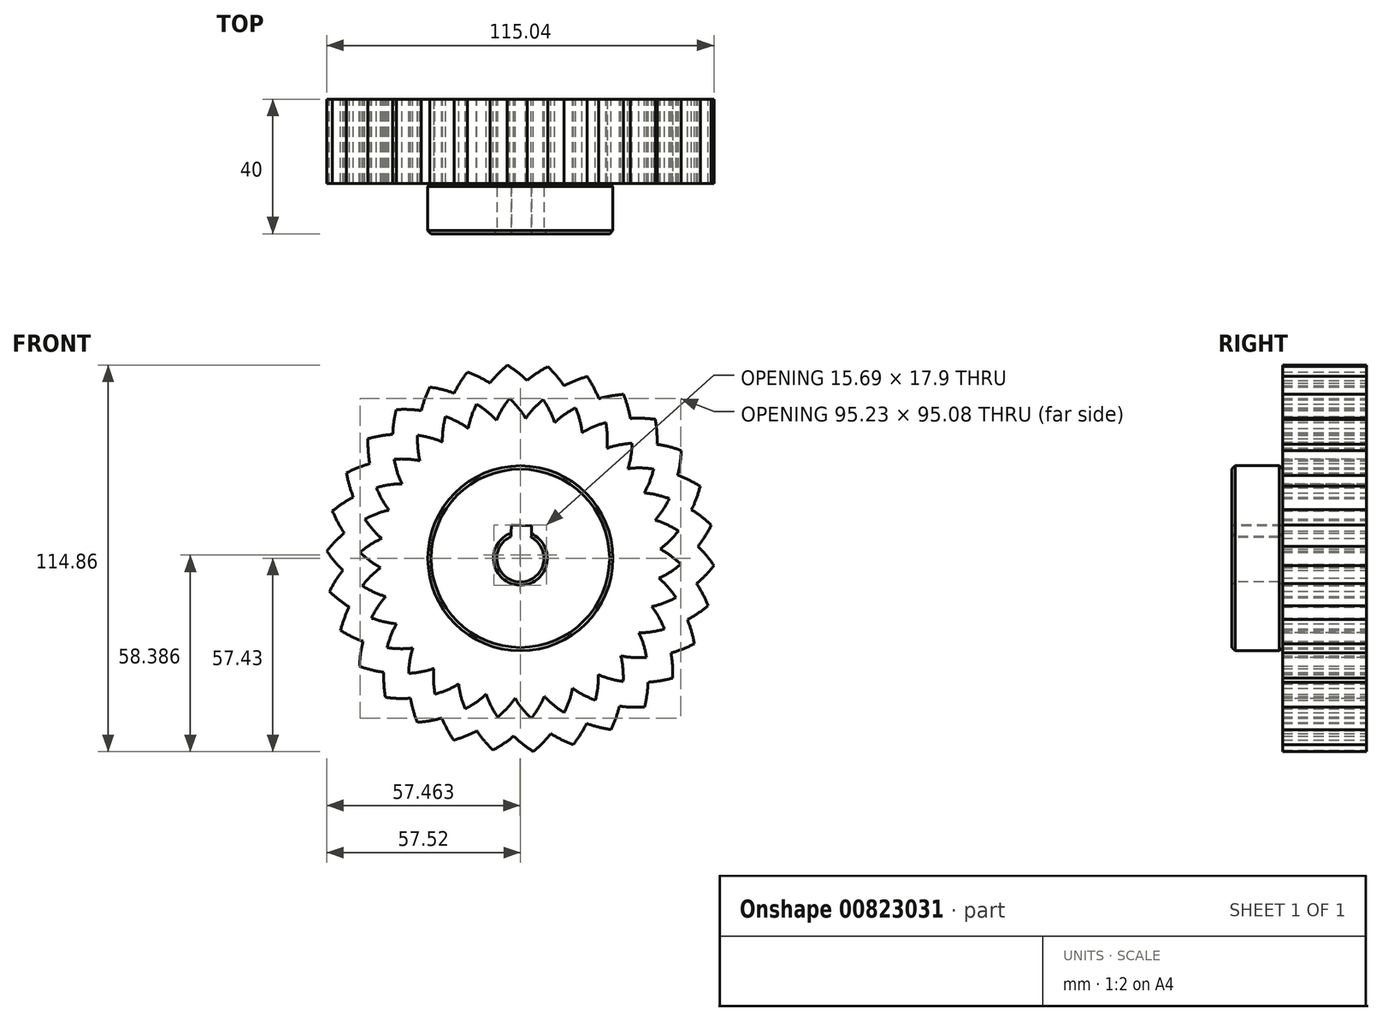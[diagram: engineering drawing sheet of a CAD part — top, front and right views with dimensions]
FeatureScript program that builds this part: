
annotation { "Feature Type Name" : "Feature", "Feature Type Description" : "" }
export const myFeature = defineFeature(function(context is Context, id is Id, definition is map)
    precondition{}
    {
        {
            var Q0;
            Q0=qCreatedBy(makeId("Front.planeOp"),FACE);
            var sketch = newSketch(context, id + "F0", { "sketchPlane" : qUnion([Q0])});
            skArc(sketch, "E0", {"start": v(-34.7, 6.12) * mm, "mid": v(-35.1, 3.07) * mm, "end": v(-35.24, 0) * mm, "construction": true});
            skLineSegment(sketch, "E1", {"start": v(0, 0) * mm, "end": v(309.01, 0) * mm, "construction": true});
            skPoint(sketch, "E2", {"position": v(35.24, 0) * mm});
            skLineSegment(sketch, "E3", {"start": v(0, 0) * mm, "end": v(-35.24, 0) * mm, "construction": true});
            skArc(sketch, "E4.trimOffspring", {"start": v(-30.6, -17.46) * mm, "mid": v(35.03, 3.83) * mm, "end": v(-33.66, 10.43) * mm, "construction": true});
            skFitSpline(sketch, "E5", {"points": [v(35.24, 0) * mm, v(35.77, 0.06) * mm, v(37.32, 0.5) * mm, v(39.74, 1.64) * mm, v(42.8, 3.8) * mm, v(46.2, 7.23) * mm, v(49.58, 12.07) * mm, v(52.5, 18.39) * mm, v(54.57, 26.16) * mm], "startDerivative": vector(10.04, 0.75) * mm, "endDerivative": vector(10.04, 44.08) * mm});
            skArc(sketch, "E6", {"start": v(34.12, 5.1) * mm, "mid": v(34, 5.9) * mm, "end": v(33.85, 6.7) * mm});
            skArc(sketch, "E7", {"start": v(39.96, 1.77) * mm, "mid": v(39.9, 2.68) * mm, "end": v(39.84, 3.6) * mm});
            skCircle(sketch, "E8", {"center": v(0, 0) * mm, "radius": 37.5 * mm, "construction": true});
            skPoint(sketch, "E9", {"position": v(37.5, 0.56) * mm});
            skPoint(sketch, "E10", {"position": v(36.56, 8.34) * mm});
            skPoint(sketch, "E11.orphan", {"position": v(37.03, 4.45) * mm});
            skLineSegment(sketch, "E12", {"start": v(37.5, 0.56) * mm, "end": v(37.03, 4.45) * mm, "construction": true});
            skLineSegment(sketch, "E13", {"start": v(37.26, 2.5) * mm, "end": v(0, 0) * mm, "construction": true});
            skFitSpline(sketch, "E14.MirrorCS", {"points": [v(34.92, 4.72) * mm, v(35.46, 4.73) * mm, v(37.05, 4.5) * mm, v(39.6, 3.7) * mm, v(42.93, 1.96) * mm, v(46.76, -0.98) * mm, v(50.74, -5.32) * mm, v(54.5, -11.2) * mm, v(57.58, -18.62) * mm], "startDerivative": vector(10.05, 0.6) * mm, "endDerivative": vector(15.85, -42.34) * mm});
            skLineSegment(sketch, "E15", {"start": v(35.24, 0) * mm, "end": v(35, 0) * mm});
            skLineSegment(sketch, "E16.MirrorCS", {"start": v(34.92, 4.72) * mm, "end": v(34.68, 4.68) * mm});
            skPoint(sketch, "E17.visualSharp", {"position": v(34.19, 4.62) * mm});
            skArc(sketch, "E17.filletArc", {"start": v(34.12, 5.1) * mm, "mid": v(34.31, 4.78) * mm, "end": v(34.68, 4.68) * mm});
            skPoint(sketch, "E18.visualSharp", {"position": v(34.5, 0) * mm});
            skArc(sketch, "E18.filletArc", {"start": v(35, 0) * mm, "mid": v(34.65, -0.14) * mm, "end": v(34.5, -0.5) * mm});
            skPoint(sketch, "E19.1.1", {"position": v(34.47, 7.33) * mm});
            skPoint(sketch, "E19.1.2", {"position": v(33.75, 7.17) * mm});
            skPoint(sketch, "E19.1.3", {"position": v(32.48, 11.62) * mm});
            skPoint(sketch, "E19.1.4", {"position": v(35.3, 12.05) * mm});
            skPoint(sketch, "E19.1.5", {"position": v(33.18, 11.87) * mm});
            skArc(sketch, "E19.1.6", {"start": v(38.72, 10.04) * mm, "mid": v(38.48, 10.92) * mm, "end": v(38.22, 11.8) * mm});
            skArc(sketch, "E19.1.8", {"start": v(32.31, 12.09) * mm, "mid": v(32.57, 11.8) * mm, "end": v(32.95, 11.8) * mm});
            skPoint(sketch, "E19.1.9", {"position": v(34.47, 7.33) * mm});
            skPoint(sketch, "E19.1.10", {"position": v(33.18, 11.87) * mm});
            skArc(sketch, "E19.1.11", {"start": v(34.23, 7.28) * mm, "mid": v(33.92, 7.06) * mm, "end": v(33.85, 6.7) * mm});
            skPoint(sketch, "E19.1.12", {"position": v(33.18, 11.87) * mm});
            skPoint(sketch, "E19.1.13", {"position": v(34.47, 7.33) * mm});
            skPoint(sketch, "E19.1.14", {"position": v(33.18, 11.87) * mm});
            skPoint(sketch, "E19.1.15", {"position": v(34.47, 7.33) * mm});
            skPoint(sketch, "E19.1.16", {"position": v(34.47, 7.33) * mm});
            skPoint(sketch, "E19.1.17", {"position": v(33.18, 11.87) * mm});
            skPoint(sketch, "E19.1.18", {"position": v(33.18, 11.87) * mm});
            skPoint(sketch, "E19.1.19", {"position": v(34.47, 7.33) * mm});
            skPoint(sketch, "E19.1.20", {"position": v(33.18, 11.87) * mm});
            skPoint(sketch, "E19.1.21", {"position": v(34.47, 7.33) * mm});
            skPoint(sketch, "E19.1.22", {"position": v(33.18, 11.87) * mm});
            skPoint(sketch, "E19.1.23", {"position": v(34.47, 7.33) * mm});
            skLineSegment(sketch, "E19.1.24", {"start": v(33.18, 11.87) * mm, "end": v(32.95, 11.8) * mm});
            skLineSegment(sketch, "E19.1.25", {"start": v(34.47, 7.33) * mm, "end": v(34.23, 7.28) * mm});
            skPoint(sketch, "E19.2.1", {"position": v(32.2, 14.33) * mm});
            skPoint(sketch, "E19.2.2", {"position": v(31.52, 14.03) * mm});
            skPoint(sketch, "E19.2.3", {"position": v(29.36, 18.12) * mm});
            skPoint(sketch, "E19.2.4", {"position": v(32.02, 19.13) * mm});
            skPoint(sketch, "E19.2.5", {"position": v(29.98, 18.51) * mm});
            skArc(sketch, "E19.2.6", {"start": v(35.79, 17.87) * mm, "mid": v(35.37, 18.68) * mm, "end": v(34.93, 19.49) * mm});
            skPoint(sketch, "E19.2.7", {"position": v(34.03, 15.76) * mm});
            skArc(sketch, "E19.2.8", {"start": v(29.1, 18.54) * mm, "mid": v(29.4, 18.32) * mm, "end": v(29.78, 18.38) * mm});
            skPoint(sketch, "E19.2.9", {"position": v(32.2, 14.33) * mm});
            skPoint(sketch, "E19.2.10", {"position": v(29.98, 18.51) * mm});
            skArc(sketch, "E19.2.11", {"start": v(31.97, 14.23) * mm, "mid": v(31.7, 13.96) * mm, "end": v(31.71, 13.58) * mm});
            skPoint(sketch, "E19.2.12", {"position": v(29.98, 18.51) * mm});
            skPoint(sketch, "E19.2.13", {"position": v(32.2, 14.33) * mm});
            skPoint(sketch, "E19.2.14", {"position": v(29.98, 18.51) * mm});
            skPoint(sketch, "E19.2.15", {"position": v(32.2, 14.33) * mm});
            skPoint(sketch, "E19.2.16", {"position": v(32.2, 14.33) * mm});
            skPoint(sketch, "E19.2.17", {"position": v(29.98, 18.51) * mm});
            skPoint(sketch, "E19.2.18", {"position": v(29.98, 18.51) * mm});
            skPoint(sketch, "E19.2.19", {"position": v(32.2, 14.33) * mm});
            skPoint(sketch, "E19.2.20", {"position": v(29.98, 18.51) * mm});
            skPoint(sketch, "E19.2.21", {"position": v(32.2, 14.33) * mm});
            skPoint(sketch, "E19.2.22", {"position": v(29.98, 18.51) * mm});
            skPoint(sketch, "E19.2.23", {"position": v(32.2, 14.33) * mm});
            skLineSegment(sketch, "E19.2.24", {"start": v(29.98, 18.51) * mm, "end": v(29.78, 18.38) * mm});
            skLineSegment(sketch, "E19.2.25", {"start": v(32.2, 14.33) * mm, "end": v(31.97, 14.23) * mm});
            skLineSegment(sketch, "E19.3.0", {"start": v(30, 22.5) * mm, "end": v(27.34, 25.37) * mm, "construction": true});
            skPoint(sketch, "E19.3.1", {"position": v(28.5, 20.71) * mm});
            skPoint(sketch, "E19.3.2", {"position": v(27.91, 20.28) * mm});
            skPoint(sketch, "E19.3.3", {"position": v(24.95, 23.83) * mm});
            skPoint(sketch, "E19.3.4", {"position": v(27.34, 25.37) * mm});
            skPoint(sketch, "E19.3.5", {"position": v(25.48, 24.34) * mm});
            skArc(sketch, "E19.3.6", {"start": v(31.29, 24.92) * mm, "mid": v(30.71, 25.63) * mm, "end": v(30.12, 26.32) * mm});
            skPoint(sketch, "E19.3.7", {"position": v(30, 22.5) * mm});
            skArc(sketch, "E19.3.8", {"start": v(24.6, 24.19) * mm, "mid": v(24.95, 24.04) * mm, "end": v(25.3, 24.17) * mm});
            skPoint(sketch, "E19.3.9", {"position": v(28.5, 20.71) * mm});
            skPoint(sketch, "E19.3.10", {"position": v(25.48, 24.34) * mm});
            skArc(sketch, "E19.3.11", {"start": v(28.31, 20.57) * mm, "mid": v(28.11, 20.25) * mm, "end": v(28.2, 19.88) * mm});
            skPoint(sketch, "E19.3.12", {"position": v(25.48, 24.34) * mm});
            skPoint(sketch, "E19.3.13", {"position": v(28.5, 20.71) * mm});
            skPoint(sketch, "E19.3.14", {"position": v(25.48, 24.34) * mm});
            skPoint(sketch, "E19.3.15", {"position": v(28.5, 20.71) * mm});
            skPoint(sketch, "E19.3.16", {"position": v(28.5, 20.71) * mm});
            skPoint(sketch, "E19.3.17", {"position": v(25.48, 24.34) * mm});
            skPoint(sketch, "E19.3.18", {"position": v(25.48, 24.34) * mm});
            skPoint(sketch, "E19.3.19", {"position": v(28.5, 20.71) * mm});
            skPoint(sketch, "E19.3.20", {"position": v(25.48, 24.34) * mm});
            skPoint(sketch, "E19.3.21", {"position": v(28.5, 20.71) * mm});
            skPoint(sketch, "E19.3.22", {"position": v(25.48, 24.34) * mm});
            skPoint(sketch, "E19.3.23", {"position": v(28.5, 20.71) * mm});
            skLineSegment(sketch, "E19.3.24", {"start": v(25.48, 24.34) * mm, "end": v(25.3, 24.17) * mm});
            skLineSegment(sketch, "E19.3.25", {"start": v(28.5, 20.71) * mm, "end": v(28.31, 20.57) * mm});
            skLineSegment(sketch, "E19.4.0", {"start": v(24.67, 28.24) * mm, "end": v(21.47, 30.5) * mm, "construction": true});
            skPoint(sketch, "E19.4.1", {"position": v(23.58, 26.19) * mm});
            skPoint(sketch, "E19.4.2", {"position": v(23.09, 25.64) * mm});
            skPoint(sketch, "E19.4.3", {"position": v(19.45, 28.5) * mm});
            skPoint(sketch, "E19.4.4", {"position": v(21.47, 30.5) * mm});
            skPoint(sketch, "E19.4.5", {"position": v(19.86, 29.1) * mm});
            skArc(sketch, "E19.4.6", {"start": v(25.42, 30.88) * mm, "mid": v(24.71, 31.45) * mm, "end": v(23.99, 32.01) * mm});
            skPoint(sketch, "E19.4.7", {"position": v(24.67, 28.24) * mm});
            skArc(sketch, "E19.4.8", {"start": v(19.04, 28.77) * mm, "mid": v(19.4, 28.7) * mm, "end": v(19.73, 28.9) * mm});
            skPoint(sketch, "E19.4.9", {"position": v(23.58, 26.19) * mm});
            skPoint(sketch, "E19.4.10", {"position": v(19.86, 29.1) * mm});
            skArc(sketch, "E19.4.11", {"start": v(23.42, 26) * mm, "mid": v(23.29, 25.65) * mm, "end": v(23.45, 25.3) * mm});
            skPoint(sketch, "E19.4.12", {"position": v(19.86, 29.1) * mm});
            skPoint(sketch, "E19.4.13", {"position": v(23.58, 26.19) * mm});
            skPoint(sketch, "E19.4.14", {"position": v(19.86, 29.1) * mm});
            skPoint(sketch, "E19.4.15", {"position": v(23.58, 26.19) * mm});
            skPoint(sketch, "E19.4.16", {"position": v(23.58, 26.19) * mm});
            skPoint(sketch, "E19.4.17", {"position": v(19.86, 29.1) * mm});
            skPoint(sketch, "E19.4.18", {"position": v(19.86, 29.1) * mm});
            skPoint(sketch, "E19.4.19", {"position": v(23.58, 26.19) * mm});
            skPoint(sketch, "E19.4.20", {"position": v(19.86, 29.1) * mm});
            skPoint(sketch, "E19.4.21", {"position": v(23.58, 26.19) * mm});
            skPoint(sketch, "E19.4.22", {"position": v(19.86, 29.1) * mm});
            skPoint(sketch, "E19.4.23", {"position": v(23.58, 26.19) * mm});
            skLineSegment(sketch, "E19.4.24", {"start": v(19.86, 29.1) * mm, "end": v(19.73, 28.9) * mm});
            skLineSegment(sketch, "E19.4.25", {"start": v(23.58, 26.19) * mm, "end": v(23.42, 26) * mm});
            skLineSegment(sketch, "E19.5.0", {"start": v(18.26, 32.75) * mm, "end": v(14.66, 34.3) * mm, "construction": true});
            skPoint(sketch, "E19.5.1", {"position": v(17.62, 30.52) * mm});
            skPoint(sketch, "E19.5.2", {"position": v(17.25, 29.88) * mm});
            skPoint(sketch, "E19.5.3", {"position": v(13.1, 31.92) * mm});
            skPoint(sketch, "E19.5.4", {"position": v(14.66, 34.3) * mm});
            skPoint(sketch, "E19.5.5", {"position": v(13.38, 32.6) * mm});
            skArc(sketch, "E19.5.6", {"start": v(18.45, 35.5) * mm, "mid": v(17.63, 35.9) * mm, "end": v(16.8, 36.3) * mm});
            skPoint(sketch, "E19.5.7", {"position": v(18.26, 32.75) * mm});
            skArc(sketch, "E19.5.8", {"start": v(12.64, 32.1) * mm, "mid": v(13.02, 32.1) * mm, "end": v(13.28, 32.38) * mm});
            skPoint(sketch, "E19.5.9", {"position": v(17.62, 30.52) * mm});
            skPoint(sketch, "E19.5.10", {"position": v(13.38, 32.6) * mm});
            skArc(sketch, "E19.5.11", {"start": v(17.5, 30.3) * mm, "mid": v(17.45, 29.93) * mm, "end": v(17.68, 29.63) * mm});
            skPoint(sketch, "E19.5.12", {"position": v(13.38, 32.6) * mm});
            skPoint(sketch, "E19.5.13", {"position": v(17.62, 30.52) * mm});
            skPoint(sketch, "E19.5.14", {"position": v(13.38, 32.6) * mm});
            skPoint(sketch, "E19.5.15", {"position": v(17.62, 30.52) * mm});
            skPoint(sketch, "E19.5.16", {"position": v(17.62, 30.52) * mm});
            skPoint(sketch, "E19.5.17", {"position": v(13.38, 32.6) * mm});
            skPoint(sketch, "E19.5.18", {"position": v(13.38, 32.6) * mm});
            skPoint(sketch, "E19.5.19", {"position": v(17.62, 30.52) * mm});
            skPoint(sketch, "E19.5.20", {"position": v(13.38, 32.6) * mm});
            skPoint(sketch, "E19.5.21", {"position": v(17.62, 30.52) * mm});
            skPoint(sketch, "E19.5.22", {"position": v(13.38, 32.6) * mm});
            skPoint(sketch, "E19.5.23", {"position": v(17.62, 30.52) * mm});
            skLineSegment(sketch, "E19.5.24", {"start": v(13.38, 32.6) * mm, "end": v(13.28, 32.38) * mm});
            skLineSegment(sketch, "E19.5.25", {"start": v(17.62, 30.52) * mm, "end": v(17.5, 30.3) * mm});
            skLineSegment(sketch, "E19.6.0", {"start": v(11.06, 35.83) * mm, "end": v(7.2, 36.6) * mm, "construction": true});
            skPoint(sketch, "E19.6.1", {"position": v(10.89, 33.51) * mm});
            skPoint(sketch, "E19.6.2", {"position": v(10.66, 32.81) * mm});
            skPoint(sketch, "E19.6.3", {"position": v(6.17, 33.94) * mm});
            skPoint(sketch, "E19.6.4", {"position": v(7.2, 36.6) * mm});
            skPoint(sketch, "E19.6.5", {"position": v(6.3, 34.67) * mm});
            skArc(sketch, "E19.6.6", {"start": v(10.67, 38.55) * mm, "mid": v(9.78, 38.79) * mm, "end": v(8.9, 39) * mm});
            skPoint(sketch, "E19.6.7", {"position": v(11.06, 35.83) * mm});
            skArc(sketch, "E19.6.8", {"start": v(5.69, 34.03) * mm, "mid": v(6.06, 34.11) * mm, "end": v(6.26, 34.43) * mm});
            skPoint(sketch, "E19.6.9", {"position": v(10.89, 33.51) * mm});
            skPoint(sketch, "E19.6.10", {"position": v(6.3, 34.67) * mm});
            skArc(sketch, "E19.6.11", {"start": v(10.81, 33.28) * mm, "mid": v(10.84, 32.9) * mm, "end": v(11.13, 32.66) * mm});
            skPoint(sketch, "E19.6.12", {"position": v(6.3, 34.67) * mm});
            skPoint(sketch, "E19.6.13", {"position": v(10.89, 33.51) * mm});
            skPoint(sketch, "E19.6.14", {"position": v(6.3, 34.67) * mm});
            skPoint(sketch, "E19.6.15", {"position": v(10.89, 33.51) * mm});
            skPoint(sketch, "E19.6.16", {"position": v(10.89, 33.51) * mm});
            skPoint(sketch, "E19.6.17", {"position": v(6.3, 34.67) * mm});
            skPoint(sketch, "E19.6.18", {"position": v(6.3, 34.67) * mm});
            skPoint(sketch, "E19.6.19", {"position": v(10.89, 33.51) * mm});
            skPoint(sketch, "E19.6.20", {"position": v(6.3, 34.67) * mm});
            skPoint(sketch, "E19.6.21", {"position": v(10.89, 33.51) * mm});
            skPoint(sketch, "E19.6.22", {"position": v(6.3, 34.67) * mm});
            skPoint(sketch, "E19.6.23", {"position": v(10.89, 33.51) * mm});
            skLineSegment(sketch, "E19.6.24", {"start": v(6.3, 34.67) * mm, "end": v(6.26, 34.43) * mm});
            skLineSegment(sketch, "E19.6.25", {"start": v(10.89, 33.51) * mm, "end": v(10.81, 33.28) * mm});
            skLineSegment(sketch, "E19.7.0", {"start": v(3.36, 37.35) * mm, "end": v(-0.56, 37.3) * mm, "construction": true});
            skPoint(sketch, "E19.7.1", {"position": v(3.68, 35.05) * mm});
            skPoint(sketch, "E19.7.2", {"position": v(3.6, 34.31) * mm});
            skPoint(sketch, "E19.7.3", {"position": v(-1.02, 34.48) * mm});
            skPoint(sketch, "E19.7.4", {"position": v(-0.56, 37.3) * mm});
            skPoint(sketch, "E19.7.5", {"position": v(-1.04, 35.22) * mm});
            skArc(sketch, "E19.7.6", {"start": v(2.42, 39.93) * mm, "mid": v(1.5, 39.97) * mm, "end": v(0.6, 40) * mm});
            skPoint(sketch, "E19.7.7", {"position": v(3.36, 37.35) * mm});
            skArc(sketch, "E19.7.8", {"start": v(-1.51, 34.47) * mm, "mid": v(-1.17, 34.63) * mm, "end": v(-1.03, 34.98) * mm});
            skPoint(sketch, "E19.7.9", {"position": v(3.68, 35.05) * mm});
            skPoint(sketch, "E19.7.10", {"position": v(-1.04, 35.22) * mm});
            skArc(sketch, "E19.7.11", {"start": v(3.66, 34.8) * mm, "mid": v(3.76, 34.44) * mm, "end": v(4.1, 34.26) * mm});
            skPoint(sketch, "E19.7.12", {"position": v(-1.04, 35.22) * mm});
            skPoint(sketch, "E19.7.13", {"position": v(3.68, 35.05) * mm});
            skPoint(sketch, "E19.7.14", {"position": v(-1.04, 35.22) * mm});
            skPoint(sketch, "E19.7.15", {"position": v(3.68, 35.05) * mm});
            skPoint(sketch, "E19.7.16", {"position": v(3.68, 35.05) * mm});
            skPoint(sketch, "E19.7.17", {"position": v(-1.04, 35.22) * mm});
            skPoint(sketch, "E19.7.18", {"position": v(-1.04, 35.22) * mm});
            skPoint(sketch, "E19.7.19", {"position": v(3.68, 35.05) * mm});
            skPoint(sketch, "E19.7.20", {"position": v(-1.04, 35.22) * mm});
            skPoint(sketch, "E19.7.21", {"position": v(3.68, 35.05) * mm});
            skPoint(sketch, "E19.7.22", {"position": v(-1.04, 35.22) * mm});
            skPoint(sketch, "E19.7.23", {"position": v(3.68, 35.05) * mm});
            skLineSegment(sketch, "E19.7.24", {"start": v(-1.04, 35.22) * mm, "end": v(-1.03, 34.98) * mm});
            skLineSegment(sketch, "E19.7.25", {"start": v(3.68, 35.05) * mm, "end": v(3.66, 34.8) * mm});
            skLineSegment(sketch, "E19.8.0", {"start": v(-4.47, 37.23) * mm, "end": v(-8.3, 36.36) * mm, "construction": true});
            skPoint(sketch, "E19.8.1", {"position": v(-3.68, 35.05) * mm});
            skPoint(sketch, "E19.8.2", {"position": v(-3.6, 34.31) * mm});
            skPoint(sketch, "E19.8.3", {"position": v(-8.17, 33.52) * mm});
            skPoint(sketch, "E19.8.4", {"position": v(-8.3, 36.36) * mm});
            skPoint(sketch, "E19.8.5", {"position": v(-8.34, 34.24) * mm});
            skArc(sketch, "E19.8.6", {"start": v(-5.94, 39.56) * mm, "mid": v(-6.84, 39.41) * mm, "end": v(-7.74, 39.24) * mm});
            skPoint(sketch, "E19.8.7", {"position": v(-4.47, 37.23) * mm});
            skArc(sketch, "E19.8.8", {"start": v(-8.64, 33.4) * mm, "mid": v(-8.34, 33.63) * mm, "end": v(-8.28, 34) * mm});
            skPoint(sketch, "E19.8.9", {"position": v(-3.68, 35.05) * mm});
            skPoint(sketch, "E19.8.10", {"position": v(-8.34, 34.24) * mm});
            skArc(sketch, "E19.8.11", {"start": v(-3.66, 34.8) * mm, "mid": v(-3.48, 34.47) * mm, "end": v(-3.12, 34.36) * mm});
            skPoint(sketch, "E19.8.12", {"position": v(-8.34, 34.24) * mm});
            skPoint(sketch, "E19.8.13", {"position": v(-3.68, 35.05) * mm});
            skPoint(sketch, "E19.8.14", {"position": v(-8.34, 34.24) * mm});
            skPoint(sketch, "E19.8.15", {"position": v(-3.68, 35.05) * mm});
            skPoint(sketch, "E19.8.16", {"position": v(-3.68, 35.05) * mm});
            skPoint(sketch, "E19.8.17", {"position": v(-8.34, 34.24) * mm});
            skPoint(sketch, "E19.8.18", {"position": v(-8.34, 34.24) * mm});
            skPoint(sketch, "E19.8.19", {"position": v(-3.68, 35.05) * mm});
            skPoint(sketch, "E19.8.20", {"position": v(-8.34, 34.24) * mm});
            skPoint(sketch, "E19.8.21", {"position": v(-3.68, 35.05) * mm});
            skPoint(sketch, "E19.8.22", {"position": v(-8.34, 34.24) * mm});
            skPoint(sketch, "E19.8.23", {"position": v(-3.68, 35.05) * mm});
            skLineSegment(sketch, "E19.8.24", {"start": v(-8.34, 34.24) * mm, "end": v(-8.28, 34) * mm});
            skLineSegment(sketch, "E19.8.25", {"start": v(-3.68, 35.05) * mm, "end": v(-3.66, 34.8) * mm});
            skLineSegment(sketch, "E19.9.0", {"start": v(-12.12, 35.49) * mm, "end": v(-15.67, 33.84) * mm, "construction": true});
            skPoint(sketch, "E19.9.1", {"position": v(-10.89, 33.51) * mm});
            skPoint(sketch, "E19.9.2", {"position": v(-10.66, 32.81) * mm});
            skPoint(sketch, "E19.9.3", {"position": v(-14.96, 31.09) * mm});
            skPoint(sketch, "E19.9.4", {"position": v(-15.67, 33.84) * mm});
            skPoint(sketch, "E19.9.5", {"position": v(-15.28, 31.76) * mm});
            skArc(sketch, "E19.9.6", {"start": v(-14.03, 37.46) * mm, "mid": v(-14.88, 37.13) * mm, "end": v(-15.73, 36.78) * mm});
            skPoint(sketch, "E19.9.7", {"position": v(-12.12, 35.49) * mm});
            skArc(sketch, "E19.9.8", {"start": v(-15.4, 30.87) * mm, "mid": v(-15.15, 31.16) * mm, "end": v(-15.17, 31.54) * mm});
            skPoint(sketch, "E19.9.9", {"position": v(-10.89, 33.51) * mm});
            skPoint(sketch, "E19.9.10", {"position": v(-15.28, 31.76) * mm});
            skArc(sketch, "E19.9.11", {"start": v(-10.81, 33.28) * mm, "mid": v(-10.57, 33) * mm, "end": v(-10.2, 32.96) * mm});
            skPoint(sketch, "E19.9.12", {"position": v(-15.28, 31.76) * mm});
            skPoint(sketch, "E19.9.13", {"position": v(-10.89, 33.51) * mm});
            skPoint(sketch, "E19.9.14", {"position": v(-15.28, 31.76) * mm});
            skPoint(sketch, "E19.9.15", {"position": v(-10.89, 33.51) * mm});
            skPoint(sketch, "E19.9.16", {"position": v(-10.89, 33.51) * mm});
            skPoint(sketch, "E19.9.17", {"position": v(-15.28, 31.76) * mm});
            skPoint(sketch, "E19.9.18", {"position": v(-15.28, 31.76) * mm});
            skPoint(sketch, "E19.9.19", {"position": v(-10.89, 33.51) * mm});
            skPoint(sketch, "E19.9.20", {"position": v(-15.28, 31.76) * mm});
            skPoint(sketch, "E19.9.21", {"position": v(-10.89, 33.51) * mm});
            skPoint(sketch, "E19.9.22", {"position": v(-15.28, 31.76) * mm});
            skPoint(sketch, "E19.9.23", {"position": v(-10.89, 33.51) * mm});
            skLineSegment(sketch, "E19.9.24", {"start": v(-15.28, 31.76) * mm, "end": v(-15.17, 31.54) * mm});
            skLineSegment(sketch, "E19.9.25", {"start": v(-10.89, 33.51) * mm, "end": v(-10.81, 33.28) * mm});
            skLineSegment(sketch, "E19.10.0", {"start": v(-19.23, 32.2) * mm, "end": v(-22.37, 29.84) * mm, "construction": true});
            skPoint(sketch, "E19.10.1", {"position": v(-17.62, 30.52) * mm});
            skPoint(sketch, "E19.10.2", {"position": v(-17.25, 29.88) * mm});
            skPoint(sketch, "E19.10.3", {"position": v(-21.1, 27.3) * mm});
            skPoint(sketch, "E19.10.4", {"position": v(-22.37, 29.84) * mm});
            skPoint(sketch, "E19.10.5", {"position": v(-21.54, 27.89) * mm});
            skArc(sketch, "E19.10.6", {"start": v(-21.51, 33.72) * mm, "mid": v(-22.28, 33.22) * mm, "end": v(-23.03, 32.7) * mm});
            skPoint(sketch, "E19.10.7", {"position": v(-19.23, 32.2) * mm});
            skArc(sketch, "E19.10.8", {"start": v(-21.48, 27) * mm, "mid": v(-21.3, 27.33) * mm, "end": v(-21.4, 27.7) * mm});
            skPoint(sketch, "E19.10.9", {"position": v(-17.62, 30.52) * mm});
            skPoint(sketch, "E19.10.10", {"position": v(-21.54, 27.89) * mm});
            skArc(sketch, "E19.10.11", {"start": v(-17.5, 30.3) * mm, "mid": v(-17.2, 30.08) * mm, "end": v(-16.82, 30.12) * mm});
            skPoint(sketch, "E19.10.12", {"position": v(-21.54, 27.89) * mm});
            skPoint(sketch, "E19.10.13", {"position": v(-17.62, 30.52) * mm});
            skPoint(sketch, "E19.10.14", {"position": v(-21.54, 27.89) * mm});
            skPoint(sketch, "E19.10.15", {"position": v(-17.62, 30.52) * mm});
            skPoint(sketch, "E19.10.16", {"position": v(-17.62, 30.52) * mm});
            skPoint(sketch, "E19.10.17", {"position": v(-21.54, 27.89) * mm});
            skPoint(sketch, "E19.10.18", {"position": v(-21.54, 27.89) * mm});
            skPoint(sketch, "E19.10.19", {"position": v(-17.62, 30.52) * mm});
            skPoint(sketch, "E19.10.20", {"position": v(-21.54, 27.89) * mm});
            skPoint(sketch, "E19.10.21", {"position": v(-17.62, 30.52) * mm});
            skPoint(sketch, "E19.10.22", {"position": v(-21.54, 27.89) * mm});
            skPoint(sketch, "E19.10.23", {"position": v(-17.62, 30.52) * mm});
            skLineSegment(sketch, "E19.10.24", {"start": v(-21.54, 27.89) * mm, "end": v(-21.4, 27.7) * mm});
            skLineSegment(sketch, "E19.10.25", {"start": v(-17.62, 30.52) * mm, "end": v(-17.5, 30.3) * mm});
            skLineSegment(sketch, "E19.11.0", {"start": v(-25.5, 27.5) * mm, "end": v(-28.08, 24.54) * mm, "construction": true});
            skPoint(sketch, "E19.11.1", {"position": v(-23.58, 26.19) * mm});
            skPoint(sketch, "E19.11.2", {"position": v(-23.09, 25.64) * mm});
            skPoint(sketch, "E19.11.3", {"position": v(-26.3, 22.32) * mm});
            skPoint(sketch, "E19.11.4", {"position": v(-28.08, 24.54) * mm});
            skPoint(sketch, "E19.11.5", {"position": v(-26.87, 22.8) * mm});
            skArc(sketch, "E19.11.6", {"start": v(-28.05, 28.51) * mm, "mid": v(-28.7, 27.86) * mm, "end": v(-29.33, 27.2) * mm});
            skPoint(sketch, "E19.11.7", {"position": v(-25.5, 27.5) * mm});
            skArc(sketch, "E19.11.8", {"start": v(-26.62, 21.94) * mm, "mid": v(-26.51, 22.3) * mm, "end": v(-26.69, 22.64) * mm});
            skPoint(sketch, "E19.11.9", {"position": v(-23.58, 26.19) * mm});
            skPoint(sketch, "E19.11.10", {"position": v(-26.87, 22.8) * mm});
            skArc(sketch, "E19.11.11", {"start": v(-23.42, 26) * mm, "mid": v(-23.08, 25.84) * mm, "end": v(-22.72, 25.97) * mm});
            skPoint(sketch, "E19.11.12", {"position": v(-26.87, 22.8) * mm});
            skPoint(sketch, "E19.11.13", {"position": v(-23.58, 26.19) * mm});
            skPoint(sketch, "E19.11.14", {"position": v(-26.87, 22.8) * mm});
            skPoint(sketch, "E19.11.15", {"position": v(-23.58, 26.19) * mm});
            skPoint(sketch, "E19.11.16", {"position": v(-23.58, 26.19) * mm});
            skPoint(sketch, "E19.11.17", {"position": v(-26.87, 22.8) * mm});
            skPoint(sketch, "E19.11.18", {"position": v(-26.87, 22.8) * mm});
            skPoint(sketch, "E19.11.19", {"position": v(-23.58, 26.19) * mm});
            skPoint(sketch, "E19.11.20", {"position": v(-26.87, 22.8) * mm});
            skPoint(sketch, "E19.11.21", {"position": v(-23.58, 26.19) * mm});
            skPoint(sketch, "E19.11.22", {"position": v(-26.87, 22.8) * mm});
            skPoint(sketch, "E19.11.23", {"position": v(-23.58, 26.19) * mm});
            skLineSegment(sketch, "E19.11.24", {"start": v(-26.87, 22.8) * mm, "end": v(-26.69, 22.64) * mm});
            skLineSegment(sketch, "E19.11.25", {"start": v(-23.58, 26.19) * mm, "end": v(-23.42, 26) * mm});
            skLineSegment(sketch, "E19.12.0", {"start": v(-30.66, 21.59) * mm, "end": v(-32.57, 18.16) * mm, "construction": true});
            skPoint(sketch, "E19.12.1", {"position": v(-28.5, 20.71) * mm});
            skPoint(sketch, "E19.12.2", {"position": v(-27.91, 20.28) * mm});
            skPoint(sketch, "E19.12.3", {"position": v(-30.37, 16.36) * mm});
            skPoint(sketch, "E19.12.4", {"position": v(-32.57, 18.16) * mm});
            skPoint(sketch, "E19.12.5", {"position": v(-31.02, 16.71) * mm});
            skArc(sketch, "E19.12.6", {"start": v(-33.37, 22.06) * mm, "mid": v(-33.86, 21.29) * mm, "end": v(-34.34, 20.5) * mm});
            skPoint(sketch, "E19.12.7", {"position": v(-30.66, 21.59) * mm});
            skArc(sketch, "E19.12.8", {"start": v(-30.6, 15.93) * mm, "mid": v(-30.57, 16.3) * mm, "end": v(-30.81, 16.6) * mm});
            skPoint(sketch, "E19.12.9", {"position": v(-28.5, 20.71) * mm});
            skPoint(sketch, "E19.12.10", {"position": v(-31.02, 16.71) * mm});
            skArc(sketch, "E19.12.11", {"start": v(-28.31, 20.57) * mm, "mid": v(-27.94, 20.48) * mm, "end": v(-27.62, 20.68) * mm});
            skPoint(sketch, "E19.12.12", {"position": v(-31.02, 16.71) * mm});
            skPoint(sketch, "E19.12.13", {"position": v(-28.5, 20.71) * mm});
            skPoint(sketch, "E19.12.14", {"position": v(-31.02, 16.71) * mm});
            skPoint(sketch, "E19.12.15", {"position": v(-28.5, 20.71) * mm});
            skPoint(sketch, "E19.12.16", {"position": v(-28.5, 20.71) * mm});
            skPoint(sketch, "E19.12.17", {"position": v(-31.02, 16.71) * mm});
            skPoint(sketch, "E19.12.18", {"position": v(-31.02, 16.71) * mm});
            skPoint(sketch, "E19.12.19", {"position": v(-28.5, 20.71) * mm});
            skPoint(sketch, "E19.12.20", {"position": v(-31.02, 16.71) * mm});
            skPoint(sketch, "E19.12.21", {"position": v(-28.5, 20.71) * mm});
            skPoint(sketch, "E19.12.22", {"position": v(-31.02, 16.71) * mm});
            skPoint(sketch, "E19.12.23", {"position": v(-28.5, 20.71) * mm});
            skLineSegment(sketch, "E19.12.24", {"start": v(-31.02, 16.71) * mm, "end": v(-30.81, 16.6) * mm});
            skLineSegment(sketch, "E19.12.25", {"start": v(-28.5, 20.71) * mm, "end": v(-28.31, 20.57) * mm});
            skLineSegment(sketch, "E19.13.0", {"start": v(-34.48, 14.74) * mm, "end": v(-35.64, 11) * mm, "construction": true});
            skPoint(sketch, "E19.13.1", {"position": v(-32.2, 14.33) * mm});
            skPoint(sketch, "E19.13.2", {"position": v(-31.52, 14.03) * mm});
            skPoint(sketch, "E19.13.3", {"position": v(-33.11, 9.69) * mm});
            skPoint(sketch, "E19.13.4", {"position": v(-35.64, 11) * mm});
            skPoint(sketch, "E19.13.5", {"position": v(-33.82, 9.9) * mm});
            skArc(sketch, "E19.13.6", {"start": v(-37.23, 14.64) * mm, "mid": v(-37.55, 13.78) * mm, "end": v(-37.86, 12.92) * mm});
            skPoint(sketch, "E19.13.7", {"position": v(-34.48, 14.74) * mm});
            skArc(sketch, "E19.13.8", {"start": v(-33.25, 9.21) * mm, "mid": v(-33.3, 9.6) * mm, "end": v(-33.59, 9.83) * mm});
            skPoint(sketch, "E19.13.9", {"position": v(-32.2, 14.33) * mm});
            skPoint(sketch, "E19.13.10", {"position": v(-33.82, 9.9) * mm});
            skArc(sketch, "E19.13.11", {"start": v(-31.97, 14.23) * mm, "mid": v(-31.6, 14.22) * mm, "end": v(-31.31, 14.48) * mm});
            skPoint(sketch, "E19.13.12", {"position": v(-33.82, 9.9) * mm});
            skPoint(sketch, "E19.13.13", {"position": v(-32.2, 14.33) * mm});
            skPoint(sketch, "E19.13.14", {"position": v(-33.82, 9.9) * mm});
            skPoint(sketch, "E19.13.15", {"position": v(-32.2, 14.33) * mm});
            skPoint(sketch, "E19.13.16", {"position": v(-32.2, 14.33) * mm});
            skPoint(sketch, "E19.13.17", {"position": v(-33.82, 9.9) * mm});
            skPoint(sketch, "E19.13.18", {"position": v(-33.82, 9.9) * mm});
            skPoint(sketch, "E19.13.19", {"position": v(-32.2, 14.33) * mm});
            skPoint(sketch, "E19.13.20", {"position": v(-33.82, 9.9) * mm});
            skPoint(sketch, "E19.13.21", {"position": v(-32.2, 14.33) * mm});
            skPoint(sketch, "E19.13.22", {"position": v(-33.82, 9.9) * mm});
            skPoint(sketch, "E19.13.23", {"position": v(-32.2, 14.33) * mm});
            skLineSegment(sketch, "E19.13.24", {"start": v(-33.82, 9.9) * mm, "end": v(-33.59, 9.83) * mm});
            skLineSegment(sketch, "E19.13.25", {"start": v(-32.2, 14.33) * mm, "end": v(-31.97, 14.23) * mm});
            skLineSegment(sketch, "E19.14.0", {"start": v(-36.8, 7.25) * mm, "end": v(-37.14, 3.35) * mm, "construction": true});
            skPoint(sketch, "E19.14.1", {"position": v(-34.47, 7.33) * mm});
            skPoint(sketch, "E19.14.2", {"position": v(-33.75, 7.17) * mm});
            skPoint(sketch, "E19.14.3", {"position": v(-34.4, 2.6) * mm});
            skPoint(sketch, "E19.14.4", {"position": v(-37.14, 3.35) * mm});
            skPoint(sketch, "E19.14.5", {"position": v(-35.14, 2.65) * mm});
            skArc(sketch, "E19.14.6", {"start": v(-39.46, 6.58) * mm, "mid": v(-39.6, 5.67) * mm, "end": v(-39.71, 4.77) * mm});
            skPoint(sketch, "E19.14.7", {"position": v(-36.8, 7.25) * mm});
            skArc(sketch, "E19.14.8", {"start": v(-34.44, 2.1) * mm, "mid": v(-34.56, 2.46) * mm, "end": v(-34.9, 2.63) * mm});
            skPoint(sketch, "E19.14.9", {"position": v(-34.47, 7.33) * mm});
            skPoint(sketch, "E19.14.10", {"position": v(-35.14, 2.65) * mm});
            skArc(sketch, "E19.14.11", {"start": v(-34.23, 7.28) * mm, "mid": v(-33.86, 7.34) * mm, "end": v(-33.64, 7.65) * mm});
            skPoint(sketch, "E19.14.12", {"position": v(-35.14, 2.65) * mm});
            skPoint(sketch, "E19.14.13", {"position": v(-34.47, 7.33) * mm});
            skPoint(sketch, "E19.14.14", {"position": v(-35.14, 2.65) * mm});
            skPoint(sketch, "E19.14.15", {"position": v(-34.47, 7.33) * mm});
            skPoint(sketch, "E19.14.16", {"position": v(-34.47, 7.33) * mm});
            skPoint(sketch, "E19.14.17", {"position": v(-35.14, 2.65) * mm});
            skPoint(sketch, "E19.14.18", {"position": v(-35.14, 2.65) * mm});
            skPoint(sketch, "E19.14.19", {"position": v(-34.47, 7.33) * mm});
            skPoint(sketch, "E19.14.20", {"position": v(-35.14, 2.65) * mm});
            skPoint(sketch, "E19.14.21", {"position": v(-34.47, 7.33) * mm});
            skPoint(sketch, "E19.14.22", {"position": v(-35.14, 2.65) * mm});
            skPoint(sketch, "E19.14.23", {"position": v(-34.47, 7.33) * mm});
            skLineSegment(sketch, "E19.14.24", {"start": v(-35.14, 2.65) * mm, "end": v(-34.9, 2.63) * mm});
            skLineSegment(sketch, "E19.14.25", {"start": v(-34.47, 7.33) * mm, "end": v(-34.23, 7.28) * mm});
            skLineSegment(sketch, "E19.15.0", {"start": v(-37.5, -0.56) * mm, "end": v(-37.03, -4.45) * mm, "construction": true});
            skPoint(sketch, "E19.15.1", {"position": v(-35.24, 0) * mm});
            skPoint(sketch, "E19.15.2", {"position": v(-34.5, 0) * mm});
            skPoint(sketch, "E19.15.3", {"position": v(-34.19, -4.62) * mm});
            skPoint(sketch, "E19.15.4", {"position": v(-37.03, -4.45) * mm});
            skPoint(sketch, "E19.15.5", {"position": v(-34.92, -4.72) * mm});
            skArc(sketch, "E19.15.6", {"start": v(-39.96, -1.77) * mm, "mid": v(-39.9, -2.68) * mm, "end": v(-39.84, -3.6) * mm});
            skPoint(sketch, "E19.15.7", {"position": v(-37.5, -0.56) * mm});
            skArc(sketch, "E19.15.8", {"start": v(-34.12, -5.1) * mm, "mid": v(-34.31, -4.78) * mm, "end": v(-34.68, -4.68) * mm});
            skPoint(sketch, "E19.15.9", {"position": v(-35.24, 0) * mm});
            skPoint(sketch, "E19.15.10", {"position": v(-34.92, -4.72) * mm});
            skArc(sketch, "E19.15.11", {"start": v(-35, 0) * mm, "mid": v(-34.65, 0.14) * mm, "end": v(-34.5, 0.5) * mm});
            skPoint(sketch, "E19.15.12", {"position": v(-34.92, -4.72) * mm});
            skPoint(sketch, "E19.15.13", {"position": v(-35.24, 0) * mm});
            skPoint(sketch, "E19.15.14", {"position": v(-34.92, -4.72) * mm});
            skPoint(sketch, "E19.15.15", {"position": v(-35.24, 0) * mm});
            skPoint(sketch, "E19.15.16", {"position": v(-35.24, 0) * mm});
            skPoint(sketch, "E19.15.17", {"position": v(-34.92, -4.72) * mm});
            skPoint(sketch, "E19.15.18", {"position": v(-34.92, -4.72) * mm});
            skPoint(sketch, "E19.15.19", {"position": v(-35.24, 0) * mm});
            skPoint(sketch, "E19.15.20", {"position": v(-34.92, -4.72) * mm});
            skPoint(sketch, "E19.15.21", {"position": v(-35.24, 0) * mm});
            skPoint(sketch, "E19.15.22", {"position": v(-34.92, -4.72) * mm});
            skPoint(sketch, "E19.15.23", {"position": v(-35.24, 0) * mm});
            skLineSegment(sketch, "E19.15.24", {"start": v(-34.92, -4.72) * mm, "end": v(-34.68, -4.68) * mm});
            skLineSegment(sketch, "E19.15.25", {"start": v(-35.24, 0) * mm, "end": v(-35, 0) * mm});
            skLineSegment(sketch, "E19.16.0", {"start": v(-36.56, -8.34) * mm, "end": v(-35.3, -12.05) * mm, "construction": true});
            skPoint(sketch, "E19.16.1", {"position": v(-34.47, -7.33) * mm});
            skPoint(sketch, "E19.16.2", {"position": v(-33.75, -7.17) * mm});
            skPoint(sketch, "E19.16.3", {"position": v(-32.48, -11.62) * mm});
            skPoint(sketch, "E19.16.4", {"position": v(-35.3, -12.05) * mm});
            skPoint(sketch, "E19.16.5", {"position": v(-33.18, -11.87) * mm});
            skArc(sketch, "E19.16.6", {"start": v(-38.72, -10.04) * mm, "mid": v(-38.48, -10.92) * mm, "end": v(-38.22, -11.8) * mm});
            skPoint(sketch, "E19.16.7", {"position": v(-36.56, -8.34) * mm});
            skArc(sketch, "E19.16.8", {"start": v(-32.31, -12.09) * mm, "mid": v(-32.57, -11.8) * mm, "end": v(-32.95, -11.8) * mm});
            skPoint(sketch, "E19.16.9", {"position": v(-34.47, -7.33) * mm});
            skPoint(sketch, "E19.16.10", {"position": v(-33.18, -11.87) * mm});
            skArc(sketch, "E19.16.11", {"start": v(-34.23, -7.28) * mm, "mid": v(-33.92, -7.06) * mm, "end": v(-33.85, -6.7) * mm});
            skPoint(sketch, "E19.16.12", {"position": v(-33.18, -11.87) * mm});
            skPoint(sketch, "E19.16.13", {"position": v(-34.47, -7.33) * mm});
            skPoint(sketch, "E19.16.14", {"position": v(-33.18, -11.87) * mm});
            skPoint(sketch, "E19.16.15", {"position": v(-34.47, -7.33) * mm});
            skPoint(sketch, "E19.16.16", {"position": v(-34.47, -7.33) * mm});
            skPoint(sketch, "E19.16.17", {"position": v(-33.18, -11.87) * mm});
            skPoint(sketch, "E19.16.18", {"position": v(-33.18, -11.87) * mm});
            skPoint(sketch, "E19.16.19", {"position": v(-34.47, -7.33) * mm});
            skPoint(sketch, "E19.16.20", {"position": v(-33.18, -11.87) * mm});
            skPoint(sketch, "E19.16.21", {"position": v(-34.47, -7.33) * mm});
            skPoint(sketch, "E19.16.22", {"position": v(-33.18, -11.87) * mm});
            skPoint(sketch, "E19.16.23", {"position": v(-34.47, -7.33) * mm});
            skLineSegment(sketch, "E19.16.24", {"start": v(-33.18, -11.87) * mm, "end": v(-32.95, -11.8) * mm});
            skLineSegment(sketch, "E19.16.25", {"start": v(-34.47, -7.33) * mm, "end": v(-34.23, -7.28) * mm});
            skLineSegment(sketch, "E19.17.0", {"start": v(-34.03, -15.76) * mm, "end": v(-32.02, -19.13) * mm, "construction": true});
            skPoint(sketch, "E19.17.1", {"position": v(-32.2, -14.33) * mm});
            skPoint(sketch, "E19.17.2", {"position": v(-31.52, -14.03) * mm});
            skPoint(sketch, "E19.17.3", {"position": v(-29.36, -18.12) * mm});
            skPoint(sketch, "E19.17.4", {"position": v(-32.02, -19.13) * mm});
            skPoint(sketch, "E19.17.5", {"position": v(-29.98, -18.51) * mm});
            skArc(sketch, "E19.17.6", {"start": v(-35.79, -17.87) * mm, "mid": v(-35.37, -18.68) * mm, "end": v(-34.93, -19.49) * mm});
            skPoint(sketch, "E19.17.7", {"position": v(-34.03, -15.76) * mm});
            skArc(sketch, "E19.17.8", {"start": v(-29.1, -18.54) * mm, "mid": v(-29.4, -18.32) * mm, "end": v(-29.78, -18.38) * mm});
            skPoint(sketch, "E19.17.9", {"position": v(-32.2, -14.33) * mm});
            skPoint(sketch, "E19.17.10", {"position": v(-29.98, -18.51) * mm});
            skArc(sketch, "E19.17.11", {"start": v(-31.97, -14.23) * mm, "mid": v(-31.7, -13.96) * mm, "end": v(-31.71, -13.58) * mm});
            skPoint(sketch, "E19.17.12", {"position": v(-29.98, -18.51) * mm});
            skPoint(sketch, "E19.17.13", {"position": v(-32.2, -14.33) * mm});
            skPoint(sketch, "E19.17.14", {"position": v(-29.98, -18.51) * mm});
            skPoint(sketch, "E19.17.15", {"position": v(-32.2, -14.33) * mm});
            skPoint(sketch, "E19.17.16", {"position": v(-32.2, -14.33) * mm});
            skPoint(sketch, "E19.17.17", {"position": v(-29.98, -18.51) * mm});
            skPoint(sketch, "E19.17.18", {"position": v(-29.98, -18.51) * mm});
            skPoint(sketch, "E19.17.19", {"position": v(-32.2, -14.33) * mm});
            skPoint(sketch, "E19.17.20", {"position": v(-29.98, -18.51) * mm});
            skPoint(sketch, "E19.17.21", {"position": v(-32.2, -14.33) * mm});
            skPoint(sketch, "E19.17.22", {"position": v(-29.98, -18.51) * mm});
            skPoint(sketch, "E19.17.23", {"position": v(-32.2, -14.33) * mm});
            skLineSegment(sketch, "E19.17.24", {"start": v(-29.98, -18.51) * mm, "end": v(-29.78, -18.38) * mm});
            skLineSegment(sketch, "E19.17.25", {"start": v(-32.2, -14.33) * mm, "end": v(-31.97, -14.23) * mm});
            skLineSegment(sketch, "E19.18.0", {"start": v(-30, -22.5) * mm, "end": v(-27.34, -25.37) * mm, "construction": true});
            skPoint(sketch, "E19.18.1", {"position": v(-28.5, -20.71) * mm});
            skPoint(sketch, "E19.18.2", {"position": v(-27.91, -20.28) * mm});
            skPoint(sketch, "E19.18.3", {"position": v(-24.95, -23.83) * mm});
            skPoint(sketch, "E19.18.4", {"position": v(-27.34, -25.37) * mm});
            skPoint(sketch, "E19.18.5", {"position": v(-25.48, -24.34) * mm});
            skArc(sketch, "E19.18.6", {"start": v(-31.29, -24.92) * mm, "mid": v(-30.71, -25.63) * mm, "end": v(-30.12, -26.32) * mm});
            skPoint(sketch, "E19.18.7", {"position": v(-30, -22.5) * mm});
            skArc(sketch, "E19.18.8", {"start": v(-24.6, -24.19) * mm, "mid": v(-24.95, -24.04) * mm, "end": v(-25.3, -24.17) * mm});
            skPoint(sketch, "E19.18.9", {"position": v(-28.5, -20.71) * mm});
            skPoint(sketch, "E19.18.10", {"position": v(-25.48, -24.34) * mm});
            skArc(sketch, "E19.18.11", {"start": v(-28.31, -20.57) * mm, "mid": v(-28.11, -20.25) * mm, "end": v(-28.2, -19.88) * mm});
            skPoint(sketch, "E19.18.12", {"position": v(-25.48, -24.34) * mm});
            skPoint(sketch, "E19.18.13", {"position": v(-28.5, -20.71) * mm});
            skPoint(sketch, "E19.18.14", {"position": v(-25.48, -24.34) * mm});
            skPoint(sketch, "E19.18.15", {"position": v(-28.5, -20.71) * mm});
            skPoint(sketch, "E19.18.16", {"position": v(-28.5, -20.71) * mm});
            skPoint(sketch, "E19.18.17", {"position": v(-25.48, -24.34) * mm});
            skPoint(sketch, "E19.18.18", {"position": v(-25.48, -24.34) * mm});
            skPoint(sketch, "E19.18.19", {"position": v(-28.5, -20.71) * mm});
            skPoint(sketch, "E19.18.20", {"position": v(-25.48, -24.34) * mm});
            skPoint(sketch, "E19.18.21", {"position": v(-28.5, -20.71) * mm});
            skPoint(sketch, "E19.18.22", {"position": v(-25.48, -24.34) * mm});
            skPoint(sketch, "E19.18.23", {"position": v(-28.5, -20.71) * mm});
            skLineSegment(sketch, "E19.18.24", {"start": v(-25.48, -24.34) * mm, "end": v(-25.3, -24.17) * mm});
            skLineSegment(sketch, "E19.18.25", {"start": v(-28.5, -20.71) * mm, "end": v(-28.31, -20.57) * mm});
            skLineSegment(sketch, "E19.19.0", {"start": v(-24.67, -28.24) * mm, "end": v(-21.47, -30.5) * mm, "construction": true});
            skPoint(sketch, "E19.19.1", {"position": v(-23.58, -26.19) * mm});
            skPoint(sketch, "E19.19.2", {"position": v(-23.09, -25.64) * mm});
            skPoint(sketch, "E19.19.3", {"position": v(-19.45, -28.5) * mm});
            skPoint(sketch, "E19.19.4", {"position": v(-21.47, -30.5) * mm});
            skPoint(sketch, "E19.19.5", {"position": v(-19.86, -29.1) * mm});
            skArc(sketch, "E19.19.6", {"start": v(-25.42, -30.88) * mm, "mid": v(-24.71, -31.45) * mm, "end": v(-23.99, -32.01) * mm});
            skPoint(sketch, "E19.19.7", {"position": v(-24.67, -28.24) * mm});
            skArc(sketch, "E19.19.8", {"start": v(-19.04, -28.77) * mm, "mid": v(-19.4, -28.7) * mm, "end": v(-19.73, -28.9) * mm});
            skPoint(sketch, "E19.19.9", {"position": v(-23.58, -26.19) * mm});
            skPoint(sketch, "E19.19.10", {"position": v(-19.86, -29.1) * mm});
            skArc(sketch, "E19.19.11", {"start": v(-23.42, -26) * mm, "mid": v(-23.29, -25.65) * mm, "end": v(-23.45, -25.3) * mm});
            skPoint(sketch, "E19.19.12", {"position": v(-19.86, -29.1) * mm});
            skPoint(sketch, "E19.19.13", {"position": v(-23.58, -26.19) * mm});
            skPoint(sketch, "E19.19.14", {"position": v(-19.86, -29.1) * mm});
            skPoint(sketch, "E19.19.15", {"position": v(-23.58, -26.19) * mm});
            skPoint(sketch, "E19.19.16", {"position": v(-23.58, -26.19) * mm});
            skPoint(sketch, "E19.19.17", {"position": v(-19.86, -29.1) * mm});
            skPoint(sketch, "E19.19.18", {"position": v(-19.86, -29.1) * mm});
            skPoint(sketch, "E19.19.19", {"position": v(-23.58, -26.19) * mm});
            skPoint(sketch, "E19.19.20", {"position": v(-19.86, -29.1) * mm});
            skPoint(sketch, "E19.19.21", {"position": v(-23.58, -26.19) * mm});
            skPoint(sketch, "E19.19.22", {"position": v(-19.86, -29.1) * mm});
            skPoint(sketch, "E19.19.23", {"position": v(-23.58, -26.19) * mm});
            skLineSegment(sketch, "E19.19.24", {"start": v(-19.86, -29.1) * mm, "end": v(-19.73, -28.9) * mm});
            skLineSegment(sketch, "E19.19.25", {"start": v(-23.58, -26.19) * mm, "end": v(-23.42, -26) * mm});
            skLineSegment(sketch, "E19.20.0", {"start": v(-18.26, -32.75) * mm, "end": v(-14.66, -34.3) * mm, "construction": true});
            skPoint(sketch, "E19.20.1", {"position": v(-17.62, -30.52) * mm});
            skPoint(sketch, "E19.20.2", {"position": v(-17.25, -29.88) * mm});
            skPoint(sketch, "E19.20.3", {"position": v(-13.1, -31.92) * mm});
            skPoint(sketch, "E19.20.4", {"position": v(-14.66, -34.3) * mm});
            skPoint(sketch, "E19.20.5", {"position": v(-13.38, -32.6) * mm});
            skArc(sketch, "E19.20.6", {"start": v(-18.45, -35.5) * mm, "mid": v(-17.63, -35.9) * mm, "end": v(-16.8, -36.3) * mm});
            skPoint(sketch, "E19.20.7", {"position": v(-18.26, -32.75) * mm});
            skArc(sketch, "E19.20.8", {"start": v(-12.64, -32.1) * mm, "mid": v(-13.02, -32.1) * mm, "end": v(-13.28, -32.38) * mm});
            skPoint(sketch, "E19.20.9", {"position": v(-17.62, -30.52) * mm});
            skPoint(sketch, "E19.20.10", {"position": v(-13.38, -32.6) * mm});
            skArc(sketch, "E19.20.11", {"start": v(-17.5, -30.3) * mm, "mid": v(-17.45, -29.93) * mm, "end": v(-17.68, -29.63) * mm});
            skPoint(sketch, "E19.20.12", {"position": v(-13.38, -32.6) * mm});
            skPoint(sketch, "E19.20.13", {"position": v(-17.62, -30.52) * mm});
            skPoint(sketch, "E19.20.14", {"position": v(-13.38, -32.6) * mm});
            skPoint(sketch, "E19.20.15", {"position": v(-17.62, -30.52) * mm});
            skPoint(sketch, "E19.20.16", {"position": v(-17.62, -30.52) * mm});
            skPoint(sketch, "E19.20.17", {"position": v(-13.38, -32.6) * mm});
            skPoint(sketch, "E19.20.18", {"position": v(-13.38, -32.6) * mm});
            skPoint(sketch, "E19.20.19", {"position": v(-17.62, -30.52) * mm});
            skPoint(sketch, "E19.20.20", {"position": v(-13.38, -32.6) * mm});
            skPoint(sketch, "E19.20.21", {"position": v(-17.62, -30.52) * mm});
            skPoint(sketch, "E19.20.22", {"position": v(-13.38, -32.6) * mm});
            skPoint(sketch, "E19.20.23", {"position": v(-17.62, -30.52) * mm});
            skLineSegment(sketch, "E19.20.24", {"start": v(-13.38, -32.6) * mm, "end": v(-13.28, -32.38) * mm});
            skLineSegment(sketch, "E19.20.25", {"start": v(-17.62, -30.52) * mm, "end": v(-17.5, -30.3) * mm});
            skLineSegment(sketch, "E19.21.0", {"start": v(-11.06, -35.83) * mm, "end": v(-7.2, -36.6) * mm, "construction": true});
            skPoint(sketch, "E19.21.1", {"position": v(-10.89, -33.51) * mm});
            skPoint(sketch, "E19.21.2", {"position": v(-10.66, -32.81) * mm});
            skPoint(sketch, "E19.21.3", {"position": v(-6.17, -33.94) * mm});
            skPoint(sketch, "E19.21.4", {"position": v(-7.2, -36.6) * mm});
            skPoint(sketch, "E19.21.5", {"position": v(-6.3, -34.67) * mm});
            skArc(sketch, "E19.21.6", {"start": v(-10.67, -38.55) * mm, "mid": v(-9.78, -38.79) * mm, "end": v(-8.9, -39) * mm});
            skPoint(sketch, "E19.21.7", {"position": v(-11.06, -35.83) * mm});
            skArc(sketch, "E19.21.8", {"start": v(-5.69, -34.03) * mm, "mid": v(-6.06, -34.11) * mm, "end": v(-6.26, -34.43) * mm});
            skPoint(sketch, "E19.21.9", {"position": v(-10.89, -33.51) * mm});
            skPoint(sketch, "E19.21.10", {"position": v(-6.3, -34.67) * mm});
            skArc(sketch, "E19.21.11", {"start": v(-10.81, -33.28) * mm, "mid": v(-10.84, -32.9) * mm, "end": v(-11.13, -32.66) * mm});
            skPoint(sketch, "E19.21.12", {"position": v(-6.3, -34.67) * mm});
            skPoint(sketch, "E19.21.13", {"position": v(-10.89, -33.51) * mm});
            skPoint(sketch, "E19.21.14", {"position": v(-6.3, -34.67) * mm});
            skPoint(sketch, "E19.21.15", {"position": v(-10.89, -33.51) * mm});
            skPoint(sketch, "E19.21.16", {"position": v(-10.89, -33.51) * mm});
            skPoint(sketch, "E19.21.17", {"position": v(-6.3, -34.67) * mm});
            skPoint(sketch, "E19.21.18", {"position": v(-6.3, -34.67) * mm});
            skPoint(sketch, "E19.21.19", {"position": v(-10.89, -33.51) * mm});
            skPoint(sketch, "E19.21.20", {"position": v(-6.3, -34.67) * mm});
            skPoint(sketch, "E19.21.21", {"position": v(-10.89, -33.51) * mm});
            skPoint(sketch, "E19.21.22", {"position": v(-6.3, -34.67) * mm});
            skPoint(sketch, "E19.21.23", {"position": v(-10.89, -33.51) * mm});
            skLineSegment(sketch, "E19.21.24", {"start": v(-6.3, -34.67) * mm, "end": v(-6.26, -34.43) * mm});
            skLineSegment(sketch, "E19.21.25", {"start": v(-10.89, -33.51) * mm, "end": v(-10.81, -33.28) * mm});
            skLineSegment(sketch, "E19.22.0", {"start": v(-3.36, -37.35) * mm, "end": v(0.56, -37.3) * mm, "construction": true});
            skPoint(sketch, "E19.22.1", {"position": v(-3.68, -35.05) * mm});
            skPoint(sketch, "E19.22.2", {"position": v(-3.6, -34.31) * mm});
            skPoint(sketch, "E19.22.3", {"position": v(1.02, -34.48) * mm});
            skPoint(sketch, "E19.22.4", {"position": v(0.56, -37.3) * mm});
            skPoint(sketch, "E19.22.5", {"position": v(1.04, -35.22) * mm});
            skArc(sketch, "E19.22.6", {"start": v(-2.42, -39.93) * mm, "mid": v(-1.5, -39.97) * mm, "end": v(-0.6, -40) * mm});
            skPoint(sketch, "E19.22.7", {"position": v(-3.36, -37.35) * mm});
            skArc(sketch, "E19.22.8", {"start": v(1.51, -34.47) * mm, "mid": v(1.17, -34.63) * mm, "end": v(1.03, -34.98) * mm});
            skPoint(sketch, "E19.22.9", {"position": v(-3.68, -35.05) * mm});
            skPoint(sketch, "E19.22.10", {"position": v(1.04, -35.22) * mm});
            skArc(sketch, "E19.22.11", {"start": v(-3.66, -34.8) * mm, "mid": v(-3.76, -34.44) * mm, "end": v(-4.1, -34.26) * mm});
            skPoint(sketch, "E19.22.12", {"position": v(1.04, -35.22) * mm});
            skPoint(sketch, "E19.22.13", {"position": v(-3.68, -35.05) * mm});
            skPoint(sketch, "E19.22.14", {"position": v(1.04, -35.22) * mm});
            skPoint(sketch, "E19.22.15", {"position": v(-3.68, -35.05) * mm});
            skPoint(sketch, "E19.22.16", {"position": v(-3.68, -35.05) * mm});
            skPoint(sketch, "E19.22.17", {"position": v(1.04, -35.22) * mm});
            skPoint(sketch, "E19.22.18", {"position": v(1.04, -35.22) * mm});
            skPoint(sketch, "E19.22.19", {"position": v(-3.68, -35.05) * mm});
            skPoint(sketch, "E19.22.20", {"position": v(1.04, -35.22) * mm});
            skPoint(sketch, "E19.22.21", {"position": v(-3.68, -35.05) * mm});
            skPoint(sketch, "E19.22.22", {"position": v(1.04, -35.22) * mm});
            skPoint(sketch, "E19.22.23", {"position": v(-3.68, -35.05) * mm});
            skLineSegment(sketch, "E19.22.24", {"start": v(1.04, -35.22) * mm, "end": v(1.03, -34.98) * mm});
            skLineSegment(sketch, "E19.22.25", {"start": v(-3.68, -35.05) * mm, "end": v(-3.66, -34.8) * mm});
            skLineSegment(sketch, "E19.23.0", {"start": v(4.47, -37.23) * mm, "end": v(8.3, -36.36) * mm, "construction": true});
            skPoint(sketch, "E19.23.1", {"position": v(3.68, -35.05) * mm});
            skPoint(sketch, "E19.23.2", {"position": v(3.6, -34.31) * mm});
            skPoint(sketch, "E19.23.3", {"position": v(8.17, -33.52) * mm});
            skPoint(sketch, "E19.23.4", {"position": v(8.3, -36.36) * mm});
            skPoint(sketch, "E19.23.5", {"position": v(8.34, -34.24) * mm});
            skArc(sketch, "E19.23.6", {"start": v(5.94, -39.56) * mm, "mid": v(6.84, -39.41) * mm, "end": v(7.74, -39.24) * mm});
            skPoint(sketch, "E19.23.7", {"position": v(4.47, -37.23) * mm});
            skArc(sketch, "E19.23.8", {"start": v(8.64, -33.4) * mm, "mid": v(8.34, -33.63) * mm, "end": v(8.28, -34) * mm});
            skPoint(sketch, "E19.23.9", {"position": v(3.68, -35.05) * mm});
            skPoint(sketch, "E19.23.10", {"position": v(8.34, -34.24) * mm});
            skArc(sketch, "E19.23.11", {"start": v(3.66, -34.8) * mm, "mid": v(3.48, -34.47) * mm, "end": v(3.12, -34.36) * mm});
            skPoint(sketch, "E19.23.12", {"position": v(8.34, -34.24) * mm});
            skPoint(sketch, "E19.23.13", {"position": v(3.68, -35.05) * mm});
            skPoint(sketch, "E19.23.14", {"position": v(8.34, -34.24) * mm});
            skPoint(sketch, "E19.23.15", {"position": v(3.68, -35.05) * mm});
            skPoint(sketch, "E19.23.16", {"position": v(3.68, -35.05) * mm});
            skPoint(sketch, "E19.23.17", {"position": v(8.34, -34.24) * mm});
            skPoint(sketch, "E19.23.18", {"position": v(8.34, -34.24) * mm});
            skPoint(sketch, "E19.23.19", {"position": v(3.68, -35.05) * mm});
            skPoint(sketch, "E19.23.20", {"position": v(8.34, -34.24) * mm});
            skPoint(sketch, "E19.23.21", {"position": v(3.68, -35.05) * mm});
            skPoint(sketch, "E19.23.22", {"position": v(8.34, -34.24) * mm});
            skPoint(sketch, "E19.23.23", {"position": v(3.68, -35.05) * mm});
            skLineSegment(sketch, "E19.23.24", {"start": v(8.34, -34.24) * mm, "end": v(8.28, -34) * mm});
            skLineSegment(sketch, "E19.23.25", {"start": v(3.68, -35.05) * mm, "end": v(3.66, -34.8) * mm});
            skLineSegment(sketch, "E19.24.0", {"start": v(12.12, -35.49) * mm, "end": v(15.67, -33.84) * mm, "construction": true});
            skPoint(sketch, "E19.24.1", {"position": v(10.89, -33.51) * mm});
            skPoint(sketch, "E19.24.2", {"position": v(10.66, -32.81) * mm});
            skPoint(sketch, "E19.24.3", {"position": v(14.96, -31.09) * mm});
            skPoint(sketch, "E19.24.4", {"position": v(15.67, -33.84) * mm});
            skPoint(sketch, "E19.24.5", {"position": v(15.28, -31.76) * mm});
            skArc(sketch, "E19.24.6", {"start": v(14.03, -37.46) * mm, "mid": v(14.88, -37.13) * mm, "end": v(15.73, -36.78) * mm});
            skPoint(sketch, "E19.24.7", {"position": v(12.12, -35.49) * mm});
            skArc(sketch, "E19.24.8", {"start": v(15.4, -30.87) * mm, "mid": v(15.15, -31.16) * mm, "end": v(15.17, -31.54) * mm});
            skPoint(sketch, "E19.24.9", {"position": v(10.89, -33.51) * mm});
            skPoint(sketch, "E19.24.10", {"position": v(15.28, -31.76) * mm});
            skArc(sketch, "E19.24.11", {"start": v(10.81, -33.28) * mm, "mid": v(10.57, -33) * mm, "end": v(10.2, -32.96) * mm});
            skPoint(sketch, "E19.24.12", {"position": v(15.28, -31.76) * mm});
            skPoint(sketch, "E19.24.13", {"position": v(10.89, -33.51) * mm});
            skPoint(sketch, "E19.24.14", {"position": v(15.28, -31.76) * mm});
            skPoint(sketch, "E19.24.15", {"position": v(10.89, -33.51) * mm});
            skPoint(sketch, "E19.24.16", {"position": v(10.89, -33.51) * mm});
            skPoint(sketch, "E19.24.17", {"position": v(15.28, -31.76) * mm});
            skPoint(sketch, "E19.24.18", {"position": v(15.28, -31.76) * mm});
            skPoint(sketch, "E19.24.19", {"position": v(10.89, -33.51) * mm});
            skPoint(sketch, "E19.24.20", {"position": v(15.28, -31.76) * mm});
            skPoint(sketch, "E19.24.21", {"position": v(10.89, -33.51) * mm});
            skPoint(sketch, "E19.24.22", {"position": v(15.28, -31.76) * mm});
            skPoint(sketch, "E19.24.23", {"position": v(10.89, -33.51) * mm});
            skLineSegment(sketch, "E19.24.24", {"start": v(15.28, -31.76) * mm, "end": v(15.17, -31.54) * mm});
            skLineSegment(sketch, "E19.24.25", {"start": v(10.89, -33.51) * mm, "end": v(10.81, -33.28) * mm});
            skLineSegment(sketch, "E19.25.0", {"start": v(19.23, -32.2) * mm, "end": v(22.37, -29.84) * mm, "construction": true});
            skPoint(sketch, "E19.25.1", {"position": v(17.62, -30.52) * mm});
            skPoint(sketch, "E19.25.2", {"position": v(17.25, -29.88) * mm});
            skPoint(sketch, "E19.25.3", {"position": v(21.1, -27.3) * mm});
            skPoint(sketch, "E19.25.4", {"position": v(22.37, -29.84) * mm});
            skPoint(sketch, "E19.25.5", {"position": v(21.54, -27.89) * mm});
            skArc(sketch, "E19.25.6", {"start": v(21.51, -33.72) * mm, "mid": v(22.28, -33.22) * mm, "end": v(23.03, -32.7) * mm});
            skPoint(sketch, "E19.25.7", {"position": v(19.23, -32.2) * mm});
            skArc(sketch, "E19.25.8", {"start": v(21.48, -27) * mm, "mid": v(21.3, -27.33) * mm, "end": v(21.4, -27.7) * mm});
            skPoint(sketch, "E19.25.9", {"position": v(17.62, -30.52) * mm});
            skPoint(sketch, "E19.25.10", {"position": v(21.54, -27.89) * mm});
            skArc(sketch, "E19.25.11", {"start": v(17.5, -30.3) * mm, "mid": v(17.2, -30.08) * mm, "end": v(16.82, -30.12) * mm});
            skPoint(sketch, "E19.25.12", {"position": v(21.54, -27.89) * mm});
            skPoint(sketch, "E19.25.13", {"position": v(17.62, -30.52) * mm});
            skPoint(sketch, "E19.25.14", {"position": v(21.54, -27.89) * mm});
            skPoint(sketch, "E19.25.15", {"position": v(17.62, -30.52) * mm});
            skPoint(sketch, "E19.25.16", {"position": v(17.62, -30.52) * mm});
            skPoint(sketch, "E19.25.17", {"position": v(21.54, -27.89) * mm});
            skPoint(sketch, "E19.25.18", {"position": v(21.54, -27.89) * mm});
            skPoint(sketch, "E19.25.19", {"position": v(17.62, -30.52) * mm});
            skPoint(sketch, "E19.25.20", {"position": v(21.54, -27.89) * mm});
            skPoint(sketch, "E19.25.21", {"position": v(17.62, -30.52) * mm});
            skPoint(sketch, "E19.25.22", {"position": v(21.54, -27.89) * mm});
            skPoint(sketch, "E19.25.23", {"position": v(17.62, -30.52) * mm});
            skLineSegment(sketch, "E19.25.24", {"start": v(21.54, -27.89) * mm, "end": v(21.4, -27.7) * mm});
            skLineSegment(sketch, "E19.25.25", {"start": v(17.62, -30.52) * mm, "end": v(17.5, -30.3) * mm});
            skLineSegment(sketch, "E19.26.0", {"start": v(25.5, -27.5) * mm, "end": v(28.08, -24.54) * mm, "construction": true});
            skPoint(sketch, "E19.26.1", {"position": v(23.58, -26.19) * mm});
            skPoint(sketch, "E19.26.2", {"position": v(23.09, -25.64) * mm});
            skPoint(sketch, "E19.26.3", {"position": v(26.3, -22.32) * mm});
            skPoint(sketch, "E19.26.4", {"position": v(28.08, -24.54) * mm});
            skPoint(sketch, "E19.26.5", {"position": v(26.87, -22.8) * mm});
            skArc(sketch, "E19.26.6", {"start": v(28.05, -28.51) * mm, "mid": v(28.7, -27.86) * mm, "end": v(29.33, -27.2) * mm});
            skPoint(sketch, "E19.26.7", {"position": v(25.5, -27.5) * mm});
            skArc(sketch, "E19.26.8", {"start": v(26.62, -21.94) * mm, "mid": v(26.51, -22.3) * mm, "end": v(26.69, -22.64) * mm});
            skPoint(sketch, "E19.26.9", {"position": v(23.58, -26.19) * mm});
            skPoint(sketch, "E19.26.10", {"position": v(26.87, -22.8) * mm});
            skArc(sketch, "E19.26.11", {"start": v(23.42, -26) * mm, "mid": v(23.08, -25.84) * mm, "end": v(22.72, -25.97) * mm});
            skPoint(sketch, "E19.26.12", {"position": v(26.87, -22.8) * mm});
            skPoint(sketch, "E19.26.13", {"position": v(23.58, -26.19) * mm});
            skPoint(sketch, "E19.26.14", {"position": v(26.87, -22.8) * mm});
            skPoint(sketch, "E19.26.15", {"position": v(23.58, -26.19) * mm});
            skPoint(sketch, "E19.26.16", {"position": v(23.58, -26.19) * mm});
            skPoint(sketch, "E19.26.17", {"position": v(26.87, -22.8) * mm});
            skPoint(sketch, "E19.26.18", {"position": v(26.87, -22.8) * mm});
            skPoint(sketch, "E19.26.19", {"position": v(23.58, -26.19) * mm});
            skPoint(sketch, "E19.26.20", {"position": v(26.87, -22.8) * mm});
            skPoint(sketch, "E19.26.21", {"position": v(23.58, -26.19) * mm});
            skPoint(sketch, "E19.26.22", {"position": v(26.87, -22.8) * mm});
            skPoint(sketch, "E19.26.23", {"position": v(23.58, -26.19) * mm});
            skLineSegment(sketch, "E19.26.24", {"start": v(26.87, -22.8) * mm, "end": v(26.69, -22.64) * mm});
            skLineSegment(sketch, "E19.26.25", {"start": v(23.58, -26.19) * mm, "end": v(23.42, -26) * mm});
            skLineSegment(sketch, "E19.27.0", {"start": v(30.66, -21.59) * mm, "end": v(32.57, -18.16) * mm, "construction": true});
            skPoint(sketch, "E19.27.1", {"position": v(28.5, -20.71) * mm});
            skPoint(sketch, "E19.27.2", {"position": v(27.91, -20.28) * mm});
            skPoint(sketch, "E19.27.3", {"position": v(30.37, -16.36) * mm});
            skPoint(sketch, "E19.27.4", {"position": v(32.57, -18.16) * mm});
            skPoint(sketch, "E19.27.5", {"position": v(31.02, -16.71) * mm});
            skArc(sketch, "E19.27.6", {"start": v(33.37, -22.06) * mm, "mid": v(33.86, -21.29) * mm, "end": v(34.34, -20.5) * mm});
            skPoint(sketch, "E19.27.7", {"position": v(30.66, -21.59) * mm});
            skArc(sketch, "E19.27.8", {"start": v(30.6, -15.93) * mm, "mid": v(30.57, -16.3) * mm, "end": v(30.81, -16.6) * mm});
            skPoint(sketch, "E19.27.9", {"position": v(28.5, -20.71) * mm});
            skPoint(sketch, "E19.27.10", {"position": v(31.02, -16.71) * mm});
            skArc(sketch, "E19.27.11", {"start": v(28.31, -20.57) * mm, "mid": v(27.94, -20.48) * mm, "end": v(27.62, -20.68) * mm});
            skPoint(sketch, "E19.27.12", {"position": v(31.02, -16.71) * mm});
            skPoint(sketch, "E19.27.13", {"position": v(28.5, -20.71) * mm});
            skPoint(sketch, "E19.27.14", {"position": v(31.02, -16.71) * mm});
            skPoint(sketch, "E19.27.15", {"position": v(28.5, -20.71) * mm});
            skPoint(sketch, "E19.27.16", {"position": v(28.5, -20.71) * mm});
            skPoint(sketch, "E19.27.17", {"position": v(31.02, -16.71) * mm});
            skPoint(sketch, "E19.27.18", {"position": v(31.02, -16.71) * mm});
            skPoint(sketch, "E19.27.19", {"position": v(28.5, -20.71) * mm});
            skPoint(sketch, "E19.27.20", {"position": v(31.02, -16.71) * mm});
            skPoint(sketch, "E19.27.21", {"position": v(28.5, -20.71) * mm});
            skPoint(sketch, "E19.27.22", {"position": v(31.02, -16.71) * mm});
            skPoint(sketch, "E19.27.23", {"position": v(28.5, -20.71) * mm});
            skLineSegment(sketch, "E19.27.24", {"start": v(31.02, -16.71) * mm, "end": v(30.81, -16.6) * mm});
            skLineSegment(sketch, "E19.27.25", {"start": v(28.5, -20.71) * mm, "end": v(28.31, -20.57) * mm});
            skLineSegment(sketch, "E19.28.0", {"start": v(34.48, -14.74) * mm, "end": v(35.64, -11) * mm, "construction": true});
            skPoint(sketch, "E19.28.1", {"position": v(32.2, -14.33) * mm});
            skPoint(sketch, "E19.28.2", {"position": v(31.52, -14.03) * mm});
            skPoint(sketch, "E19.28.3", {"position": v(33.11, -9.69) * mm});
            skPoint(sketch, "E19.28.4", {"position": v(35.64, -11) * mm});
            skPoint(sketch, "E19.28.5", {"position": v(33.82, -9.9) * mm});
            skArc(sketch, "E19.28.6", {"start": v(37.23, -14.64) * mm, "mid": v(37.55, -13.78) * mm, "end": v(37.86, -12.92) * mm});
            skPoint(sketch, "E19.28.7", {"position": v(34.48, -14.74) * mm});
            skArc(sketch, "E19.28.8", {"start": v(33.25, -9.21) * mm, "mid": v(33.3, -9.6) * mm, "end": v(33.59, -9.83) * mm});
            skPoint(sketch, "E19.28.9", {"position": v(32.2, -14.33) * mm});
            skPoint(sketch, "E19.28.10", {"position": v(33.82, -9.9) * mm});
            skArc(sketch, "E19.28.11", {"start": v(31.97, -14.23) * mm, "mid": v(31.6, -14.22) * mm, "end": v(31.31, -14.48) * mm});
            skPoint(sketch, "E19.28.12", {"position": v(33.82, -9.9) * mm});
            skPoint(sketch, "E19.28.13", {"position": v(32.2, -14.33) * mm});
            skPoint(sketch, "E19.28.14", {"position": v(33.82, -9.9) * mm});
            skPoint(sketch, "E19.28.15", {"position": v(32.2, -14.33) * mm});
            skPoint(sketch, "E19.28.16", {"position": v(32.2, -14.33) * mm});
            skPoint(sketch, "E19.28.17", {"position": v(33.82, -9.9) * mm});
            skPoint(sketch, "E19.28.18", {"position": v(33.82, -9.9) * mm});
            skPoint(sketch, "E19.28.19", {"position": v(32.2, -14.33) * mm});
            skPoint(sketch, "E19.28.20", {"position": v(33.82, -9.9) * mm});
            skPoint(sketch, "E19.28.21", {"position": v(32.2, -14.33) * mm});
            skPoint(sketch, "E19.28.22", {"position": v(33.82, -9.9) * mm});
            skPoint(sketch, "E19.28.23", {"position": v(32.2, -14.33) * mm});
            skLineSegment(sketch, "E19.28.24", {"start": v(33.82, -9.9) * mm, "end": v(33.59, -9.83) * mm});
            skLineSegment(sketch, "E19.28.25", {"start": v(32.2, -14.33) * mm, "end": v(31.97, -14.23) * mm});
            skLineSegment(sketch, "E19.29.0", {"start": v(36.8, -7.25) * mm, "end": v(37.14, -3.35) * mm, "construction": true});
            skPoint(sketch, "E19.29.1", {"position": v(34.47, -7.33) * mm});
            skPoint(sketch, "E19.29.2", {"position": v(33.75, -7.17) * mm});
            skPoint(sketch, "E19.29.3", {"position": v(34.4, -2.6) * mm});
            skPoint(sketch, "E19.29.4", {"position": v(37.14, -3.35) * mm});
            skPoint(sketch, "E19.29.5", {"position": v(35.14, -2.65) * mm});
            skArc(sketch, "E19.29.6", {"start": v(39.46, -6.58) * mm, "mid": v(39.6, -5.67) * mm, "end": v(39.71, -4.77) * mm});
            skPoint(sketch, "E19.29.7", {"position": v(36.8, -7.25) * mm});
            skArc(sketch, "E19.29.8", {"start": v(34.44, -2.1) * mm, "mid": v(34.56, -2.46) * mm, "end": v(34.9, -2.63) * mm});
            skPoint(sketch, "E19.29.9", {"position": v(34.47, -7.33) * mm});
            skPoint(sketch, "E19.29.10", {"position": v(35.14, -2.65) * mm});
            skArc(sketch, "E19.29.11", {"start": v(34.23, -7.28) * mm, "mid": v(33.86, -7.34) * mm, "end": v(33.64, -7.65) * mm});
            skPoint(sketch, "E19.29.12", {"position": v(35.14, -2.65) * mm});
            skPoint(sketch, "E19.29.13", {"position": v(34.47, -7.33) * mm});
            skPoint(sketch, "E19.29.14", {"position": v(35.14, -2.65) * mm});
            skPoint(sketch, "E19.29.15", {"position": v(34.47, -7.33) * mm});
            skPoint(sketch, "E19.29.16", {"position": v(34.47, -7.33) * mm});
            skPoint(sketch, "E19.29.17", {"position": v(35.14, -2.65) * mm});
            skPoint(sketch, "E19.29.18", {"position": v(35.14, -2.65) * mm});
            skPoint(sketch, "E19.29.19", {"position": v(34.47, -7.33) * mm});
            skPoint(sketch, "E19.29.20", {"position": v(35.14, -2.65) * mm});
            skPoint(sketch, "E19.29.21", {"position": v(34.47, -7.33) * mm});
            skPoint(sketch, "E19.29.22", {"position": v(35.14, -2.65) * mm});
            skPoint(sketch, "E19.29.23", {"position": v(34.47, -7.33) * mm});
            skLineSegment(sketch, "E19.29.24", {"start": v(35.14, -2.65) * mm, "end": v(34.9, -2.63) * mm});
            skLineSegment(sketch, "E19.29.25", {"start": v(34.47, -7.33) * mm, "end": v(34.23, -7.28) * mm});
            skLineSegment(sketch, "E20", {"start": v(39.2, 6.8) * mm, "end": v(0, 0) * mm, "construction": true});
            skFitSpline(sketch, "E21.MirrorCS", {"points": [v(34.47, 7.33) * mm, v(34.98, 7.5) * mm, v(36.4, 8.24) * mm, v(38.53, 9.87) * mm, v(41.08, 12.62) * mm, v(43.7, 16.68) * mm, v(45.98, 22.11) * mm, v(47.54, 28.9) * mm, v(47.94, 36.93) * mm], "startDerivative": vector(9.66, 2.82) * mm, "endDerivative": vector(0.66, 45.2) * mm});
            skFitSpline(sketch, "E22.MirrorCS", {"points": [v(33.18, 11.87) * mm, v(33.7, 12) * mm, v(35.3, 12.1) * mm, v(37.97, 11.85) * mm, v(41.59, 10.84) * mm, v(45.94, 8.76) * mm, v(50.74, 5.34) * mm, v(55.63, 0.38) * mm, v(60.2, -6.24) * mm], "startDerivative": vector(9.7, 2.67) * mm, "endDerivative": vector(24.31, -38.12) * mm});
            skArc(sketch, "E23.trimOffspring", {"start": v(32.31, 12.09) * mm, "mid": v(32.02, 12.84) * mm, "end": v(31.71, 13.58) * mm});
            skLineSegment(sketch, "E24.1.0", {"start": v(36.92, 14.8) * mm, "end": v(0, 0) * mm, "construction": true});
            skLineSegment(sketch, "E24.2.0", {"start": v(33.04, 22.16) * mm, "end": v(0, 0) * mm, "construction": true});
            skLineSegment(sketch, "E24.3.0", {"start": v(27.71, 28.54) * mm, "end": v(0, 0) * mm, "construction": true});
            skLineSegment(sketch, "E24.4.0", {"start": v(21.17, 33.68) * mm, "end": v(0, 0) * mm, "construction": true});
            skLineSegment(sketch, "E24.5.0", {"start": v(13.7, 37.34) * mm, "end": v(0, 0) * mm, "construction": true});
            skLineSegment(sketch, "E24.6.0", {"start": v(5.64, 39.38) * mm, "end": v(0, 0) * mm, "construction": true});
            skLineSegment(sketch, "E24.7.0", {"start": v(-2.67, 39.7) * mm, "end": v(0, 0) * mm, "construction": true});
            skLineSegment(sketch, "E24.8.0", {"start": v(-10.86, 38.27) * mm, "end": v(0, 0) * mm, "construction": true});
            skLineSegment(sketch, "E24.9.0", {"start": v(-18.58, 35.17) * mm, "end": v(0, 0) * mm, "construction": true});
            skLineSegment(sketch, "E24.10.0", {"start": v(-25.49, 30.54) * mm, "end": v(0, 0) * mm, "construction": true});
            skLineSegment(sketch, "E24.11.0", {"start": v(-31.28, 24.58) * mm, "end": v(0, 0) * mm, "construction": true});
            skLineSegment(sketch, "E24.12.0", {"start": v(-35.7, 17.54) * mm, "end": v(0, 0) * mm, "construction": true});
            skLineSegment(sketch, "E24.13.0", {"start": v(-38.57, 9.73) * mm, "end": v(0, 0) * mm, "construction": true});
            skLineSegment(sketch, "E24.14.0", {"start": v(-39.75, 1.5) * mm, "end": v(0, 0) * mm, "construction": true});
            skLineSegment(sketch, "E24.15.0", {"start": v(-39.2, -6.8) * mm, "end": v(0, 0) * mm, "construction": true});
            skLineSegment(sketch, "E24.16.0", {"start": v(-36.92, -14.8) * mm, "end": v(0, 0) * mm, "construction": true});
            skLineSegment(sketch, "E24.17.0", {"start": v(-33.04, -22.16) * mm, "end": v(0, 0) * mm, "construction": true});
            skLineSegment(sketch, "E24.18.0", {"start": v(-27.71, -28.54) * mm, "end": v(0, 0) * mm, "construction": true});
            skLineSegment(sketch, "E24.19.0", {"start": v(-21.17, -33.68) * mm, "end": v(0, 0) * mm, "construction": true});
            skLineSegment(sketch, "E24.20.0", {"start": v(-13.7, -37.34) * mm, "end": v(0, 0) * mm, "construction": true});
            skLineSegment(sketch, "E24.21.0", {"start": v(-5.64, -39.38) * mm, "end": v(0, 0) * mm, "construction": true});
            skLineSegment(sketch, "E24.22.0", {"start": v(2.67, -39.7) * mm, "end": v(0, 0) * mm, "construction": true});
            skLineSegment(sketch, "E24.23.0", {"start": v(10.86, -38.27) * mm, "end": v(0, 0) * mm, "construction": true});
            skLineSegment(sketch, "E24.24.0", {"start": v(18.58, -35.17) * mm, "end": v(0, 0) * mm, "construction": true});
            skLineSegment(sketch, "E24.25.0", {"start": v(25.49, -30.54) * mm, "end": v(0, 0) * mm, "construction": true});
            skLineSegment(sketch, "E24.26.0", {"start": v(31.28, -24.58) * mm, "end": v(0, 0) * mm, "construction": true});
            skLineSegment(sketch, "E24.27.0", {"start": v(35.7, -17.54) * mm, "end": v(0, 0) * mm, "construction": true});
            skLineSegment(sketch, "E24.28.0", {"start": v(38.57, -9.73) * mm, "end": v(0, 0) * mm, "construction": true});
            skLineSegment(sketch, "E24.29.0", {"start": v(39.75, -1.5) * mm, "end": v(0, 0) * mm, "construction": true});
            skFitSpline(sketch, "E25.MirrorCS", {"points": [v(25.48, 24.34) * mm, v(25.9, 24.66) * mm, v(27.33, 25.42) * mm, v(29.87, 26.27) * mm, v(33.58, 26.82) * mm, v(38.4, 26.7) * mm, v(44.18, 25.52) * mm, v(50.67, 22.97) * mm, v(57.53, 18.78) * mm], "startDerivative": vector(7.78, 6.39) * mm, "endDerivative": vector(37.71, -24.94) * mm});
            skFitSpline(sketch, "E26.MirrorCS", {"points": [v(28.5, 20.71) * mm, v(28.9, 21.08) * mm, v(29.9, 22.34) * mm, v(31.19, 24.69) * mm, v(32.4, 28.24) * mm, v(33.13, 33) * mm, v(33.01, 38.9) * mm, v(31.67, 45.74) * mm, v(28.77, 53.24) * mm], "startDerivative": vector(7.68, 6.5) * mm, "endDerivative": vector(-17.78, 41.57) * mm});
            skFitSpline(sketch, "E27.MirrorCS", {"points": [v(29.98, 18.51) * mm, v(30.47, 18.74) * mm, v(32.02, 19.19) * mm, v(34.68, 19.48) * mm, v(38.42, 19.25) * mm, v(43.11, 18.12) * mm, v(48.52, 15.78) * mm, v(54.34, 11.94) * mm, v(60.18, 6.4) * mm], "startDerivative": vector(8.94, 4.63) * mm, "endDerivative": vector(31.7, -32.23) * mm});
            skFitSpline(sketch, "E28.MirrorCS", {"points": [v(32.2, 14.33) * mm, v(32.65, 14.6) * mm, v(33.9, 15.63) * mm, v(35.64, 17.66) * mm, v(37.56, 20.89) * mm, v(39.27, 25.4) * mm, v(40.38, 31.19) * mm, v(40.49, 38.16) * mm, v(39.21, 46.1) * mm], "startDerivative": vector(8.86, 4.77) * mm, "endDerivative": vector(-8.75, 44.36) * mm});
            skFitSpline(sketch, "E29.MirrorCS", {"points": [v(-1.04, 35.22) * mm, v(-1, 35.76) * mm, v(-0.6, 37.32) * mm, v(0.47, 39.77) * mm, v(2.54, 42.9) * mm, v(5.86, 46.4) * mm, v(10.6, 49.91) * mm, v(16.83, 53.03) * mm, v(24.54, 55.32) * mm], "startDerivative": vector(0.46, 10.05) * mm, "endDerivative": vector(43.77, 11.34) * mm});
            skFitSpline(sketch, "E30.MirrorCS", {"points": [v(3.68, 35.05) * mm, v(3.68, 35.58) * mm, v(3.4, 37.17) * mm, v(2.52, 39.7) * mm, v(0.69, 42.97) * mm, v(-2.36, 46.7) * mm, v(-6.82, 50.57) * mm, v(-12.8, 54.14) * mm, v(-20.31, 57) * mm], "startDerivative": vector(0.3, 10.06) * mm, "endDerivative": vector(-42.8, 14.6) * mm});
            skFitSpline(sketch, "E31.MirrorCS", {"points": [v(6.3, 34.67) * mm, v(6.46, 35.18) * mm, v(7.17, 36.63) * mm, v(8.73, 38.8) * mm, v(11.4, 41.43) * mm, v(15.38, 44.17) * mm, v(20.74, 46.62) * mm, v(27.49, 48.37) * mm, v(35.5, 49) * mm], "startDerivative": vector(2.54, 9.74) * mm, "endDerivative": vector(45.17, 2) * mm});
            skFitSpline(sketch, "E32.MirrorCS", {"points": [v(10.89, 33.51) * mm, v(11, 34.04) * mm, v(11.06, 35.65) * mm, v(10.72, 38.3) * mm, v(9.6, 41.89) * mm, v(7.4, 46.18) * mm, v(3.84, 50.88) * mm, v(-1.26, 55.62) * mm, v(-8.02, 59.98) * mm], "startDerivative": vector(2.39, 9.78) * mm, "endDerivative": vector(-38.82, 23.18) * mm});
            skFitSpline(sketch, "E33.MirrorCS", {"points": [v(13.38, 32.6) * mm, v(13.64, 33.07) * mm, v(14.62, 34.34) * mm, v(16.6, 36.14) * mm, v(19.77, 38.16) * mm, v(24.23, 40) * mm, v(29.98, 41.28) * mm, v(36.94, 41.6) * mm, v(44.92, 40.56) * mm], "startDerivative": vector(4.5, 9) * mm, "endDerivative": vector(44.6, -7.44) * mm});
            skFitSpline(sketch, "E34.MirrorCS", {"points": [v(17.62, 30.52) * mm, v(17.83, 31) * mm, v(18.23, 32.57) * mm, v(18.45, 35.24) * mm, v(18.1, 38.97) * mm, v(16.84, 43.63) * mm, v(14.34, 48.97) * mm, v(10.33, 54.67) * mm, v(4.63, 60.34) * mm], "startDerivative": vector(4.37, 9.07) * mm, "endDerivative": vector(-33.15, 30.74) * mm});
            skFitSpline(sketch, "E35.MirrorCS", {"points": [v(19.86, 29.1) * mm, v(20.21, 29.51) * mm, v(21.44, 30.55) * mm, v(23.76, 31.9) * mm, v(27.27, 33.21) * mm, v(32.02, 34.1) * mm, v(37.91, 34.15) * mm, v(44.79, 33) * mm, v(52.37, 30.33) * mm], "startDerivative": vector(6.28, 7.87) * mm, "endDerivative": vector(42.07, -16.55) * mm});
            skFitSpline(sketch, "E36.MirrorCS", {"points": [v(23.58, 26.19) * mm, v(23.89, 26.62) * mm, v(24.6, 28.06) * mm, v(25.37, 30.63) * mm, v(25.81, 34.36) * mm, v(25.55, 39.18) * mm, v(24.2, 44.92) * mm, v(21.47, 51.32) * mm, v(17.08, 58.06) * mm], "startDerivative": vector(6.16, 7.96) * mm, "endDerivative": vector(-26.04, 36.96) * mm});
            skFitSpline(sketch, "E37.MirrorCS", {"points": [v(-34.92, -4.72) * mm, v(-35.46, -4.73) * mm, v(-37.05, -4.5) * mm, v(-39.6, -3.7) * mm, v(-42.93, -1.96) * mm, v(-46.76, 0.98) * mm, v(-50.74, 5.32) * mm, v(-54.5, 11.2) * mm, v(-57.58, 18.62) * mm], "startDerivative": vector(-10.05, -0.6) * mm, "endDerivative": vector(-15.85, 42.34) * mm});
            skFitSpline(sketch, "E38.MirrorCS", {"points": [v(-35.24, 0) * mm, v(-35.77, -0.06) * mm, v(-37.32, -0.5) * mm, v(-39.74, -1.64) * mm, v(-42.8, -3.8) * mm, v(-46.2, -7.23) * mm, v(-49.58, -12.07) * mm, v(-52.5, -18.39) * mm, v(-54.57, -26.16) * mm], "startDerivative": vector(-10.04, -0.75) * mm, "endDerivative": vector(-10.04, -44.08) * mm});
            skFitSpline(sketch, "E39.MirrorCS", {"points": [v(-35.14, 2.65) * mm, v(-35.67, 2.75) * mm, v(-37.18, 3.3) * mm, v(-39.5, 4.62) * mm, v(-42.4, 7.01) * mm, v(-45.53, 10.68) * mm, v(-48.53, 15.76) * mm, v(-50.98, 22.28) * mm, v(-52.45, 30.19) * mm], "startDerivative": vector(-9.95, 1.5) * mm, "endDerivative": vector(-6.7, 44.71) * mm});
            skFitSpline(sketch, "E40.MirrorCS", {"points": [v(-34.47, 7.33) * mm, v(-35, 7.38) * mm, v(-36.6, 7.28) * mm, v(-39.22, 6.66) * mm, v(-42.66, 5.18) * mm, v(-46.7, 2.54) * mm, v(-51, -1.5) * mm, v(-55.18, -7.07) * mm, v(-58.82, -14.24) * mm], "startDerivative": vector(-9.97, 1.35) * mm, "endDerivative": vector(-19, -41.03) * mm});
            skFitSpline(sketch, "E41.MirrorCS", {"points": [v(-33.82, 9.9) * mm, v(-34.31, 10.1) * mm, v(-35.68, 10.95) * mm, v(-37.68, 12.74) * mm, v(-40.02, 15.67) * mm, v(-42.32, 19.91) * mm, v(-44.2, 25.5) * mm, v(-45.23, 32.4) * mm, v(-45.03, 40.43) * mm], "startDerivative": vector(-9.42, 3.54) * mm, "endDerivative": vector(2.74, 45.13) * mm});
            skFitSpline(sketch, "E42.MirrorCS", {"points": [v(-32.2, 14.33) * mm, v(-32.7, 14.5) * mm, v(-34.3, 14.73) * mm, v(-36.97, 14.67) * mm, v(-40.65, 13.93) * mm, v(-45.15, 12.2) * mm, v(-50.2, 9.14) * mm, v(-55.45, 4.56) * mm, v(-60.5, -1.7) * mm], "startDerivative": vector(-9.47, 3.4) * mm, "endDerivative": vector(-27.1, -36.19) * mm});
            skPoint(sketch, "E43.MirrorP", {"position": v(-32.75, 18.27) * mm});
            skFitSpline(sketch, "E44.MirrorCS", {"points": [v(-28.5, 20.71) * mm, v(-28.98, 20.98) * mm, v(-30.48, 21.54) * mm, v(-33.12, 22.03) * mm, v(-36.87, 22.08) * mm, v(-41.63, 21.31) * mm, v(-47.2, 19.38) * mm, v(-53.29, 15.98) * mm, v(-59.53, 10.91) * mm], "startDerivative": vector(-8.56, 5.3) * mm, "endDerivative": vector(-34.04, -29.76) * mm});
            skFitSpline(sketch, "E45.MirrorCS", {"points": [v(-26.87, 22.8) * mm, v(-27.24, 23.19) * mm, v(-28.14, 24.52) * mm, v(-29.24, 26.96) * mm, v(-30.18, 30.6) * mm, v(-30.56, 35.4) * mm, v(-30, 41.27) * mm, v(-28.14, 47.99) * mm, v(-24.7, 55.25) * mm], "startDerivative": vector(-7.17, 7.07) * mm, "endDerivative": vector(20.86, 40.11) * mm});
            skFitSpline(sketch, "E46.MirrorCS", {"points": [v(-23.58, 26.19) * mm, v(-23.98, 26.54) * mm, v(-25.34, 27.4) * mm, v(-27.81, 28.44) * mm, v(-31.47, 29.26) * mm, v(-36.3, 29.5) * mm, v(-42.14, 28.77) * mm, v(-48.8, 26.71) * mm, v(-55.96, 23.05) * mm], "startDerivative": vector(-7.27, 6.96) * mm, "endDerivative": vector(-39.48, -22.03) * mm});
            skFitSpline(sketch, "E47.MirrorCS", {"points": [v(-21.54, 27.89) * mm, v(-21.82, 28.34) * mm, v(-22.43, 29.83) * mm, v(-23, 32.45) * mm, v(-23.16, 36.2) * mm, v(-22.53, 40.98) * mm, v(-20.76, 46.6) * mm, v(-17.55, 52.8) * mm, v(-12.66, 59.18) * mm], "startDerivative": vector(-5.54, 8.4) * mm, "endDerivative": vector(28.74, 34.9) * mm});
            skFitSpline(sketch, "E48.MirrorCS", {"points": [v(-17.62, 30.52) * mm, v(-17.94, 30.95) * mm, v(-19.09, 32.07) * mm, v(-21.3, 33.6) * mm, v(-24.7, 35.17) * mm, v(-29.36, 36.4) * mm, v(-35.24, 36.9) * mm, v(-42.18, 36.28) * mm, v(-49.94, 34.18) * mm], "startDerivative": vector(-5.67, 8.32) * mm, "endDerivative": vector(-43.2, -13.34) * mm});
            skFitSpline(sketch, "E49.MirrorCS", {"points": [v(-15.28, 31.76) * mm, v(-15.45, 32.26) * mm, v(-15.73, 33.85) * mm, v(-15.75, 36.53) * mm, v(-15.13, 40.23) * mm, v(-13.52, 44.77) * mm, v(-10.62, 49.9) * mm, v(-6.2, 55.29) * mm, v(-0.08, 60.52) * mm], "startDerivative": vector(-3.67, 9.37) * mm, "endDerivative": vector(35.37, 28.16) * mm});
            skFitSpline(sketch, "E50.MirrorCS", {"points": [v(-10.89, 33.51) * mm, v(-11.11, 34) * mm, v(-12, 35.34) * mm, v(-13.84, 37.3) * mm, v(-16.85, 39.54) * mm, v(-21.15, 41.71) * mm, v(-26.8, 43.42) * mm, v(-33.71, 44.25) * mm, v(-41.74, 43.82) * mm], "startDerivative": vector(-3.82, 9.31) * mm, "endDerivative": vector(-45.03, -4.07) * mm});
            skFitSpline(sketch, "E51.MirrorCS", {"points": [v(-8.34, 34.24) * mm, v(-8.4, 34.77) * mm, v(-8.35, 36.38) * mm, v(-7.81, 39) * mm, v(-6.43, 42.5) * mm, v(-3.91, 46.6) * mm, v(0, 51.02) * mm, v(5.44, 55.37) * mm, v(12.5, 59.21) * mm], "startDerivative": vector(-1.65, 9.93) * mm, "endDerivative": vector(40.45, 20.2) * mm});
            skFitSpline(sketch, "E52.MirrorCS", {"points": [v(-3.68, 35.05) * mm, v(-3.8, 35.57) * mm, v(-4.4, 37.06) * mm, v(-5.79, 39.35) * mm, v(-8.26, 42.17) * mm, v(-12.02, 45.2) * mm, v(-17.18, 48.04) * mm, v(-23.78, 50.3) * mm, v(-31.72, 51.54) * mm], "startDerivative": vector(-1.8, 9.9) * mm, "endDerivative": vector(-44.9, 5.38) * mm});
            skFitSpline(sketch, "E53.MirrorCS", {"points": [v(8.34, -34.24) * mm, v(8.4, -34.77) * mm, v(8.35, -36.38) * mm, v(7.81, -39) * mm, v(6.43, -42.5) * mm, v(3.91, -46.6) * mm, v(0, -51.02) * mm, v(-5.44, -55.37) * mm, v(-12.5, -59.21) * mm], "startDerivative": vector(1.65, -9.93) * mm, "endDerivative": vector(-40.45, -20.2) * mm});
            skFitSpline(sketch, "E54.MirrorCS", {"points": [v(3.68, -35.05) * mm, v(3.8, -35.57) * mm, v(4.4, -37.06) * mm, v(5.79, -39.35) * mm, v(8.26, -42.17) * mm, v(12.02, -45.2) * mm, v(17.18, -48.04) * mm, v(23.78, -50.3) * mm, v(31.72, -51.54) * mm], "startDerivative": vector(1.8, -9.9) * mm, "endDerivative": vector(44.9, -5.38) * mm});
            skFitSpline(sketch, "E55.MirrorCS", {"points": [v(1.04, -35.22) * mm, v(1, -35.76) * mm, v(0.6, -37.32) * mm, v(-0.47, -39.77) * mm, v(-2.54, -42.9) * mm, v(-5.86, -46.4) * mm, v(-10.6, -49.91) * mm, v(-16.83, -53.03) * mm, v(-24.54, -55.32) * mm], "startDerivative": vector(-0.46, -10.05) * mm, "endDerivative": vector(-43.77, -11.34) * mm});
            skFitSpline(sketch, "E56.MirrorCS", {"points": [v(-3.68, -35.05) * mm, v(-3.68, -35.58) * mm, v(-3.4, -37.17) * mm, v(-2.52, -39.7) * mm, v(-0.69, -42.97) * mm, v(2.36, -46.7) * mm, v(6.82, -50.57) * mm, v(12.8, -54.14) * mm, v(20.31, -57) * mm], "startDerivative": vector(-0.3, -10.06) * mm, "endDerivative": vector(42.8, -14.6) * mm});
            skFitSpline(sketch, "E57.MirrorCS", {"points": [v(-6.3, -34.67) * mm, v(-6.46, -35.18) * mm, v(-7.17, -36.63) * mm, v(-8.73, -38.8) * mm, v(-11.4, -41.43) * mm, v(-15.38, -44.17) * mm, v(-20.74, -46.62) * mm, v(-27.49, -48.37) * mm, v(-35.5, -49) * mm], "startDerivative": vector(-2.54, -9.74) * mm, "endDerivative": vector(-45.17, -2) * mm});
            skFitSpline(sketch, "E58.MirrorCS", {"points": [v(-10.89, -33.51) * mm, v(-11, -34.04) * mm, v(-11.06, -35.65) * mm, v(-10.72, -38.3) * mm, v(-9.6, -41.89) * mm, v(-7.4, -46.18) * mm, v(-3.84, -50.88) * mm, v(1.26, -55.62) * mm, v(8.02, -59.98) * mm], "startDerivative": vector(-2.39, -9.78) * mm, "endDerivative": vector(38.82, -23.18) * mm});
            skFitSpline(sketch, "E59.MirrorCS", {"points": [v(-13.38, -32.6) * mm, v(-13.64, -33.07) * mm, v(-14.62, -34.34) * mm, v(-16.6, -36.14) * mm, v(-19.77, -38.16) * mm, v(-24.23, -40) * mm, v(-29.98, -41.28) * mm, v(-36.94, -41.6) * mm, v(-44.92, -40.56) * mm], "startDerivative": vector(-4.5, -9) * mm, "endDerivative": vector(-44.6, 7.44) * mm});
            skFitSpline(sketch, "E60.MirrorCS", {"points": [v(-17.62, -30.52) * mm, v(-17.83, -31) * mm, v(-18.23, -32.57) * mm, v(-18.45, -35.24) * mm, v(-18.1, -38.97) * mm, v(-16.84, -43.63) * mm, v(-14.34, -48.97) * mm, v(-10.33, -54.67) * mm, v(-4.63, -60.34) * mm], "startDerivative": vector(-4.37, -9.07) * mm, "endDerivative": vector(33.15, -30.74) * mm});
            skFitSpline(sketch, "E61.MirrorCS", {"points": [v(-19.86, -29.1) * mm, v(-20.21, -29.51) * mm, v(-21.44, -30.55) * mm, v(-23.76, -31.9) * mm, v(-27.27, -33.21) * mm, v(-32.02, -34.1) * mm, v(-37.91, -34.15) * mm, v(-44.79, -33) * mm, v(-52.37, -30.33) * mm], "startDerivative": vector(-6.28, -7.87) * mm, "endDerivative": vector(-42.07, 16.55) * mm});
            skFitSpline(sketch, "E62.MirrorCS", {"points": [v(-25.48, -24.34) * mm, v(-25.9, -24.66) * mm, v(-27.33, -25.42) * mm, v(-29.87, -26.27) * mm, v(-33.58, -26.82) * mm, v(-38.4, -26.7) * mm, v(-44.18, -25.52) * mm, v(-50.67, -22.97) * mm, v(-57.53, -18.78) * mm], "startDerivative": vector(-7.78, -6.39) * mm, "endDerivative": vector(-37.71, 24.94) * mm});
            skFitSpline(sketch, "E63.MirrorCS", {"points": [v(-28.5, -20.71) * mm, v(-28.9, -21.08) * mm, v(-29.9, -22.34) * mm, v(-31.19, -24.69) * mm, v(-32.4, -28.24) * mm, v(-33.13, -33) * mm, v(-33.01, -38.9) * mm, v(-31.67, -45.74) * mm, v(-28.77, -53.24) * mm], "startDerivative": vector(-7.68, -6.5) * mm, "endDerivative": vector(17.78, -41.57) * mm});
            skFitSpline(sketch, "E64.MirrorCS", {"points": [v(-29.98, -18.51) * mm, v(-30.47, -18.74) * mm, v(-32.02, -19.19) * mm, v(-34.68, -19.48) * mm, v(-38.42, -19.25) * mm, v(-43.11, -18.12) * mm, v(-48.52, -15.78) * mm, v(-54.34, -11.94) * mm, v(-60.18, -6.4) * mm], "startDerivative": vector(-8.94, -4.63) * mm, "endDerivative": vector(-31.7, 32.23) * mm});
            skFitSpline(sketch, "E65.MirrorCS", {"points": [v(-32.2, -14.33) * mm, v(-32.65, -14.6) * mm, v(-33.9, -15.63) * mm, v(-35.64, -17.66) * mm, v(-37.56, -20.89) * mm, v(-39.27, -25.4) * mm, v(-40.38, -31.19) * mm, v(-40.49, -38.16) * mm, v(-39.21, -46.1) * mm], "startDerivative": vector(-8.86, -4.77) * mm, "endDerivative": vector(8.75, -44.36) * mm});
            skFitSpline(sketch, "E66.MirrorCS", {"points": [v(-33.18, -11.87) * mm, v(-33.7, -12) * mm, v(-35.3, -12.1) * mm, v(-37.97, -11.85) * mm, v(-41.59, -10.84) * mm, v(-45.94, -8.76) * mm, v(-50.74, -5.34) * mm, v(-55.63, -0.38) * mm, v(-60.2, 6.24) * mm], "startDerivative": vector(-9.7, -2.67) * mm, "endDerivative": vector(-24.31, 38.12) * mm});
            skFitSpline(sketch, "E67.MirrorCS", {"points": [v(-34.47, -7.33) * mm, v(-34.98, -7.5) * mm, v(-36.4, -8.24) * mm, v(-38.53, -9.87) * mm, v(-41.08, -12.62) * mm, v(-43.7, -16.68) * mm, v(-45.98, -22.11) * mm, v(-47.54, -28.9) * mm, v(-47.94, -36.93) * mm], "startDerivative": vector(-9.66, -2.82) * mm, "endDerivative": vector(-0.66, -45.2) * mm});
            skFitSpline(sketch, "E68.MirrorCS", {"points": [v(-31.02, 16.71) * mm, v(-31.46, 17.02) * mm, v(-32.62, 18.13) * mm, v(-34.21, 20.3) * mm, v(-35.88, 23.65) * mm, v(-37.25, 28.28) * mm, v(-37.92, 34.13) * mm, v(-37.5, 41.1) * mm, v(-35.64, 48.91) * mm], "startDerivative": vector(-8.48, 5.42) * mm, "endDerivative": vector(12.06, 43.57) * mm});
            skFitSpline(sketch, "E69.MirrorCS", {"points": [v(-23.58, -26.19) * mm, v(-23.89, -26.62) * mm, v(-24.6, -28.06) * mm, v(-25.37, -30.63) * mm, v(-25.81, -34.36) * mm, v(-25.55, -39.18) * mm, v(-24.2, -44.92) * mm, v(-21.47, -51.32) * mm, v(-17.08, -58.06) * mm], "startDerivative": vector(-6.16, -7.96) * mm, "endDerivative": vector(26.04, -36.96) * mm});
            skFitSpline(sketch, "E70.MirrorCS", {"points": [v(35.14, -2.65) * mm, v(35.67, -2.75) * mm, v(37.18, -3.3) * mm, v(39.5, -4.62) * mm, v(42.4, -7.01) * mm, v(45.53, -10.68) * mm, v(48.53, -15.76) * mm, v(50.98, -22.28) * mm, v(52.45, -30.19) * mm], "startDerivative": vector(9.95, -1.5) * mm, "endDerivative": vector(6.7, -44.71) * mm});
            skFitSpline(sketch, "E71.MirrorCS", {"points": [v(34.47, -7.33) * mm, v(35, -7.38) * mm, v(36.6, -7.28) * mm, v(39.22, -6.66) * mm, v(42.66, -5.18) * mm, v(46.7, -2.54) * mm, v(51, 1.5) * mm, v(55.18, 7.07) * mm, v(58.82, 14.24) * mm], "startDerivative": vector(9.97, -1.35) * mm, "endDerivative": vector(19, 41.03) * mm});
            skFitSpline(sketch, "E72.MirrorCS", {"points": [v(33.82, -9.9) * mm, v(34.31, -10.1) * mm, v(35.68, -10.95) * mm, v(37.68, -12.74) * mm, v(40.02, -15.67) * mm, v(42.32, -19.91) * mm, v(44.2, -25.5) * mm, v(45.23, -32.4) * mm, v(45.03, -40.43) * mm], "startDerivative": vector(9.42, -3.54) * mm, "endDerivative": vector(-2.74, -45.13) * mm});
            skFitSpline(sketch, "E73.MirrorCS", {"points": [v(32.2, -14.33) * mm, v(32.7, -14.5) * mm, v(34.3, -14.73) * mm, v(36.97, -14.67) * mm, v(40.65, -13.93) * mm, v(45.15, -12.2) * mm, v(50.2, -9.14) * mm, v(55.45, -4.56) * mm, v(60.5, 1.7) * mm], "startDerivative": vector(9.47, -3.4) * mm, "endDerivative": vector(27.1, 36.19) * mm});
            skFitSpline(sketch, "E74.MirrorCS", {"points": [v(31.02, -16.71) * mm, v(31.46, -17.02) * mm, v(32.62, -18.13) * mm, v(34.21, -20.3) * mm, v(35.88, -23.65) * mm, v(37.25, -28.28) * mm, v(37.92, -34.13) * mm, v(37.5, -41.1) * mm, v(35.64, -48.91) * mm], "startDerivative": vector(8.48, -5.42) * mm, "endDerivative": vector(-12.06, -43.57) * mm});
            skFitSpline(sketch, "E75.MirrorCS", {"points": [v(28.5, -20.71) * mm, v(28.98, -20.98) * mm, v(30.48, -21.54) * mm, v(33.12, -22.03) * mm, v(36.87, -22.08) * mm, v(41.63, -21.31) * mm, v(47.2, -19.38) * mm, v(53.29, -15.98) * mm, v(59.53, -10.91) * mm], "startDerivative": vector(8.56, -5.3) * mm, "endDerivative": vector(34.04, 29.76) * mm});
            skFitSpline(sketch, "E76.MirrorCS", {"points": [v(26.87, -22.8) * mm, v(27.24, -23.19) * mm, v(28.14, -24.52) * mm, v(29.24, -26.96) * mm, v(30.18, -30.6) * mm, v(30.56, -35.4) * mm, v(30, -41.27) * mm, v(28.14, -47.99) * mm, v(24.7, -55.25) * mm], "startDerivative": vector(7.17, -7.07) * mm, "endDerivative": vector(-20.86, -40.11) * mm});
            skFitSpline(sketch, "E77.MirrorCS", {"points": [v(23.58, -26.19) * mm, v(23.98, -26.54) * mm, v(25.34, -27.4) * mm, v(27.81, -28.44) * mm, v(31.47, -29.26) * mm, v(36.3, -29.5) * mm, v(42.14, -28.77) * mm, v(48.8, -26.71) * mm, v(55.96, -23.05) * mm], "startDerivative": vector(7.27, -6.96) * mm, "endDerivative": vector(39.48, 22.03) * mm});
            skFitSpline(sketch, "E78.MirrorCS", {"points": [v(21.54, -27.89) * mm, v(21.82, -28.34) * mm, v(22.43, -29.83) * mm, v(23, -32.45) * mm, v(23.16, -36.2) * mm, v(22.53, -40.98) * mm, v(20.76, -46.6) * mm, v(17.55, -52.8) * mm, v(12.66, -59.18) * mm], "startDerivative": vector(5.54, -8.4) * mm, "endDerivative": vector(-28.74, -34.9) * mm});
            skFitSpline(sketch, "E79.MirrorCS", {"points": [v(17.62, -30.52) * mm, v(17.94, -30.95) * mm, v(19.09, -32.07) * mm, v(21.3, -33.6) * mm, v(24.7, -35.17) * mm, v(29.36, -36.4) * mm, v(35.24, -36.9) * mm, v(42.18, -36.28) * mm, v(49.94, -34.18) * mm], "startDerivative": vector(5.67, -8.32) * mm, "endDerivative": vector(43.2, 13.34) * mm});
            skFitSpline(sketch, "E80.MirrorCS", {"points": [v(15.28, -31.76) * mm, v(15.45, -32.26) * mm, v(15.73, -33.85) * mm, v(15.75, -36.53) * mm, v(15.13, -40.23) * mm, v(13.52, -44.77) * mm, v(10.62, -49.9) * mm, v(6.2, -55.29) * mm, v(0.08, -60.52) * mm], "startDerivative": vector(3.67, -9.37) * mm, "endDerivative": vector(-35.37, -28.16) * mm});
            skFitSpline(sketch, "E81.MirrorCS", {"points": [v(10.89, -33.51) * mm, v(11.11, -34) * mm, v(12, -35.34) * mm, v(13.84, -37.3) * mm, v(16.85, -39.54) * mm, v(21.15, -41.71) * mm, v(26.8, -43.42) * mm, v(33.71, -44.25) * mm, v(41.74, -43.82) * mm], "startDerivative": vector(3.82, -9.31) * mm, "endDerivative": vector(45.03, 4.07) * mm});
            skArc(sketch, "E82.trimOffspring", {"start": v(29.1, 18.54) * mm, "mid": v(28.65, 19.21) * mm, "end": v(28.2, 19.88) * mm});
            skArc(sketch, "E83.trimOffspring", {"start": v(27.91, 20.28) * mm, "mid": v(-32.89, -10.43) * mm, "end": v(34.5, -0.5) * mm});
            skSolve(sketch);
        }
        {
            var Q0;
            Q0=qSketchRegion(id+"F0",true);
            extrude(context, id + "F1", {"entities" : qUnion([Q0]), "depth" : 25 * mm, "offsetDistance" : 25 * mm});
        }
        {
            var Q0;
            Q0=makeQuery(id+"F1.opExtrude","CAP_FACE",FACE,{"disambiguationData":[OSD([sQuery(id+"F0.wireOp",EDGE,"E5"),sQuery(id+"F0.wireOp",EDGE,"E6"),sQuery(id+"F0.wireOp",EDGE,"E7"),sQuery(id+"F0.wireOp",EDGE,"E14.MirrorCS"),sQuery(id+"F0.wireOp",EDGE,"E15"),sQuery(id+"F0.wireOp",EDGE,"E16.MirrorCS"),sQuery(id+"F0.wireOp",EDGE,"E17.filletArc"),sQuery(id+"F0.wireOp",EDGE,"E18.filletArc"),sQuery(id+"F0.wireOp",EDGE,"E19.1.6"),sQuery(id+"F0.wireOp",EDGE,"E19.1.8"),sQuery(id+"F0.wireOp",EDGE,"E19.1.11"),sQuery(id+"F0.wireOp",EDGE,"E19.1.24"),sQuery(id+"F0.wireOp",EDGE,"E19.1.25"),sQuery(id+"F0.wireOp",EDGE,"E19.2.6"),sQuery(id+"F0.wireOp",EDGE,"E19.2.8"),sQuery(id+"F0.wireOp",EDGE,"E19.2.11"),sQuery(id+"F0.wireOp",EDGE,"E19.2.24"),sQuery(id+"F0.wireOp",EDGE,"E19.2.25"),sQuery(id+"F0.wireOp",EDGE,"E19.3.6"),sQuery(id+"F0.wireOp",EDGE,"E19.3.8"),sQuery(id+"F0.wireOp",EDGE,"E19.3.11"),sQuery(id+"F0.wireOp",EDGE,"E19.3.24"),sQuery(id+"F0.wireOp",EDGE,"E19.3.25"),sQuery(id+"F0.wireOp",EDGE,"E19.4.6"),sQuery(id+"F0.wireOp",EDGE,"E19.4.8"),sQuery(id+"F0.wireOp",EDGE,"E19.4.11"),sQuery(id+"F0.wireOp",EDGE,"E19.4.24"),sQuery(id+"F0.wireOp",EDGE,"E19.4.25"),sQuery(id+"F0.wireOp",EDGE,"E19.5.6"),sQuery(id+"F0.wireOp",EDGE,"E19.5.8"),sQuery(id+"F0.wireOp",EDGE,"E19.5.11"),sQuery(id+"F0.wireOp",EDGE,"E19.5.24"),sQuery(id+"F0.wireOp",EDGE,"E19.5.25"),sQuery(id+"F0.wireOp",EDGE,"E19.6.6"),sQuery(id+"F0.wireOp",EDGE,"E19.6.8"),sQuery(id+"F0.wireOp",EDGE,"E19.6.11"),sQuery(id+"F0.wireOp",EDGE,"E19.6.24"),sQuery(id+"F0.wireOp",EDGE,"E19.6.25"),sQuery(id+"F0.wireOp",EDGE,"E19.7.6"),sQuery(id+"F0.wireOp",EDGE,"E19.7.8"),sQuery(id+"F0.wireOp",EDGE,"E19.7.11"),sQuery(id+"F0.wireOp",EDGE,"E19.7.24"),sQuery(id+"F0.wireOp",EDGE,"E19.7.25"),sQuery(id+"F0.wireOp",EDGE,"E19.8.6"),sQuery(id+"F0.wireOp",EDGE,"E19.8.8"),sQuery(id+"F0.wireOp",EDGE,"E19.8.11"),sQuery(id+"F0.wireOp",EDGE,"E19.8.24"),sQuery(id+"F0.wireOp",EDGE,"E19.8.25"),sQuery(id+"F0.wireOp",EDGE,"E19.9.6"),sQuery(id+"F0.wireOp",EDGE,"E19.9.8"),sQuery(id+"F0.wireOp",EDGE,"E19.9.11"),sQuery(id+"F0.wireOp",EDGE,"E19.9.24"),sQuery(id+"F0.wireOp",EDGE,"E19.9.25"),sQuery(id+"F0.wireOp",EDGE,"E19.10.6"),sQuery(id+"F0.wireOp",EDGE,"E19.10.8"),sQuery(id+"F0.wireOp",EDGE,"E19.10.11"),sQuery(id+"F0.wireOp",EDGE,"E19.10.24"),sQuery(id+"F0.wireOp",EDGE,"E19.10.25"),sQuery(id+"F0.wireOp",EDGE,"E19.11.6"),sQuery(id+"F0.wireOp",EDGE,"E19.11.8"),sQuery(id+"F0.wireOp",EDGE,"E19.11.11"),sQuery(id+"F0.wireOp",EDGE,"E19.11.24"),sQuery(id+"F0.wireOp",EDGE,"E19.11.25"),sQuery(id+"F0.wireOp",EDGE,"E19.12.6"),sQuery(id+"F0.wireOp",EDGE,"E19.12.8"),sQuery(id+"F0.wireOp",EDGE,"E19.12.11"),sQuery(id+"F0.wireOp",EDGE,"E19.12.24"),sQuery(id+"F0.wireOp",EDGE,"E19.12.25"),sQuery(id+"F0.wireOp",EDGE,"E19.13.6"),sQuery(id+"F0.wireOp",EDGE,"E19.13.8"),sQuery(id+"F0.wireOp",EDGE,"E19.13.11"),sQuery(id+"F0.wireOp",EDGE,"E19.13.24"),sQuery(id+"F0.wireOp",EDGE,"E19.13.25"),sQuery(id+"F0.wireOp",EDGE,"E19.14.6"),sQuery(id+"F0.wireOp",EDGE,"E19.14.8"),sQuery(id+"F0.wireOp",EDGE,"E19.14.11"),sQuery(id+"F0.wireOp",EDGE,"E19.14.24"),sQuery(id+"F0.wireOp",EDGE,"E19.14.25"),sQuery(id+"F0.wireOp",EDGE,"E19.15.6"),sQuery(id+"F0.wireOp",EDGE,"E19.15.8"),sQuery(id+"F0.wireOp",EDGE,"E19.15.11"),sQuery(id+"F0.wireOp",EDGE,"E19.15.24"),sQuery(id+"F0.wireOp",EDGE,"E19.15.25"),sQuery(id+"F0.wireOp",EDGE,"E19.16.6"),sQuery(id+"F0.wireOp",EDGE,"E19.16.8"),sQuery(id+"F0.wireOp",EDGE,"E19.16.11"),sQuery(id+"F0.wireOp",EDGE,"E19.16.24"),sQuery(id+"F0.wireOp",EDGE,"E19.16.25"),sQuery(id+"F0.wireOp",EDGE,"E19.17.6"),sQuery(id+"F0.wireOp",EDGE,"E19.17.8"),sQuery(id+"F0.wireOp",EDGE,"E19.17.11"),sQuery(id+"F0.wireOp",EDGE,"E19.17.24"),sQuery(id+"F0.wireOp",EDGE,"E19.17.25"),sQuery(id+"F0.wireOp",EDGE,"E19.18.6"),sQuery(id+"F0.wireOp",EDGE,"E19.18.8"),sQuery(id+"F0.wireOp",EDGE,"E19.18.11"),sQuery(id+"F0.wireOp",EDGE,"E19.18.24"),sQuery(id+"F0.wireOp",EDGE,"E19.18.25"),sQuery(id+"F0.wireOp",EDGE,"E19.19.6"),sQuery(id+"F0.wireOp",EDGE,"E19.19.8"),sQuery(id+"F0.wireOp",EDGE,"E19.19.11"),sQuery(id+"F0.wireOp",EDGE,"E19.19.24"),sQuery(id+"F0.wireOp",EDGE,"E19.19.25"),sQuery(id+"F0.wireOp",EDGE,"E19.20.6"),sQuery(id+"F0.wireOp",EDGE,"E19.20.8"),sQuery(id+"F0.wireOp",EDGE,"E19.20.11"),sQuery(id+"F0.wireOp",EDGE,"E19.20.24"),sQuery(id+"F0.wireOp",EDGE,"E19.20.25"),sQuery(id+"F0.wireOp",EDGE,"E19.21.6"),sQuery(id+"F0.wireOp",EDGE,"E19.21.8"),sQuery(id+"F0.wireOp",EDGE,"E19.21.11"),sQuery(id+"F0.wireOp",EDGE,"E19.21.24"),sQuery(id+"F0.wireOp",EDGE,"E19.21.25"),sQuery(id+"F0.wireOp",EDGE,"E19.22.6"),sQuery(id+"F0.wireOp",EDGE,"E19.22.8"),sQuery(id+"F0.wireOp",EDGE,"E19.22.11"),sQuery(id+"F0.wireOp",EDGE,"E19.22.24"),sQuery(id+"F0.wireOp",EDGE,"E19.22.25"),sQuery(id+"F0.wireOp",EDGE,"E19.23.6"),sQuery(id+"F0.wireOp",EDGE,"E19.23.8"),sQuery(id+"F0.wireOp",EDGE,"E19.23.11"),sQuery(id+"F0.wireOp",EDGE,"E19.23.24"),sQuery(id+"F0.wireOp",EDGE,"E19.23.25"),sQuery(id+"F0.wireOp",EDGE,"E19.24.6"),sQuery(id+"F0.wireOp",EDGE,"E19.24.8"),sQuery(id+"F0.wireOp",EDGE,"E19.24.11"),sQuery(id+"F0.wireOp",EDGE,"E19.24.24"),sQuery(id+"F0.wireOp",EDGE,"E19.24.25"),sQuery(id+"F0.wireOp",EDGE,"E19.25.6"),sQuery(id+"F0.wireOp",EDGE,"E19.25.8"),sQuery(id+"F0.wireOp",EDGE,"E19.25.11"),sQuery(id+"F0.wireOp",EDGE,"E19.25.24"),sQuery(id+"F0.wireOp",EDGE,"E19.25.25"),sQuery(id+"F0.wireOp",EDGE,"E19.26.6"),sQuery(id+"F0.wireOp",EDGE,"E19.26.8"),sQuery(id+"F0.wireOp",EDGE,"E19.26.11"),sQuery(id+"F0.wireOp",EDGE,"E19.26.24"),sQuery(id+"F0.wireOp",EDGE,"E19.26.25"),sQuery(id+"F0.wireOp",EDGE,"E19.27.6"),sQuery(id+"F0.wireOp",EDGE,"E19.27.8"),sQuery(id+"F0.wireOp",EDGE,"E19.27.11"),sQuery(id+"F0.wireOp",EDGE,"E19.27.24"),sQuery(id+"F0.wireOp",EDGE,"E19.27.25"),sQuery(id+"F0.wireOp",EDGE,"E19.28.6"),sQuery(id+"F0.wireOp",EDGE,"E19.28.8"),sQuery(id+"F0.wireOp",EDGE,"E19.28.11"),sQuery(id+"F0.wireOp",EDGE,"E19.28.24"),sQuery(id+"F0.wireOp",EDGE,"E19.28.25"),sQuery(id+"F0.wireOp",EDGE,"E19.29.6"),sQuery(id+"F0.wireOp",EDGE,"E19.29.8"),sQuery(id+"F0.wireOp",EDGE,"E19.29.11"),sQuery(id+"F0.wireOp",EDGE,"E19.29.24"),sQuery(id+"F0.wireOp",EDGE,"E19.29.25"),sQuery(id+"F0.wireOp",EDGE,"E21.MirrorCS"),sQuery(id+"F0.wireOp",EDGE,"E22.MirrorCS"),sQuery(id+"F0.wireOp",EDGE,"E23.trimOffspring"),sQuery(id+"F0.wireOp",EDGE,"E25.MirrorCS"),sQuery(id+"F0.wireOp",EDGE,"E26.MirrorCS"),sQuery(id+"F0.wireOp",EDGE,"E27.MirrorCS"),sQuery(id+"F0.wireOp",EDGE,"E28.MirrorCS"),sQuery(id+"F0.wireOp",EDGE,"E29.MirrorCS"),sQuery(id+"F0.wireOp",EDGE,"E30.MirrorCS"),sQuery(id+"F0.wireOp",EDGE,"E31.MirrorCS"),sQuery(id+"F0.wireOp",EDGE,"E32.MirrorCS"),sQuery(id+"F0.wireOp",EDGE,"E33.MirrorCS"),sQuery(id+"F0.wireOp",EDGE,"E34.MirrorCS"),sQuery(id+"F0.wireOp",EDGE,"E35.MirrorCS"),sQuery(id+"F0.wireOp",EDGE,"E36.MirrorCS"),sQuery(id+"F0.wireOp",EDGE,"E37.MirrorCS"),sQuery(id+"F0.wireOp",EDGE,"E38.MirrorCS"),sQuery(id+"F0.wireOp",EDGE,"E39.MirrorCS"),sQuery(id+"F0.wireOp",EDGE,"E40.MirrorCS"),sQuery(id+"F0.wireOp",EDGE,"E41.MirrorCS"),sQuery(id+"F0.wireOp",EDGE,"E42.MirrorCS"),sQuery(id+"F0.wireOp",EDGE,"E44.MirrorCS"),sQuery(id+"F0.wireOp",EDGE,"E45.MirrorCS"),sQuery(id+"F0.wireOp",EDGE,"E46.MirrorCS"),sQuery(id+"F0.wireOp",EDGE,"E47.MirrorCS"),sQuery(id+"F0.wireOp",EDGE,"E48.MirrorCS"),sQuery(id+"F0.wireOp",EDGE,"E49.MirrorCS"),sQuery(id+"F0.wireOp",EDGE,"E50.MirrorCS"),sQuery(id+"F0.wireOp",EDGE,"E51.MirrorCS"),sQuery(id+"F0.wireOp",EDGE,"E52.MirrorCS"),sQuery(id+"F0.wireOp",EDGE,"E53.MirrorCS"),sQuery(id+"F0.wireOp",EDGE,"E54.MirrorCS"),sQuery(id+"F0.wireOp",EDGE,"E55.MirrorCS"),sQuery(id+"F0.wireOp",EDGE,"E56.MirrorCS"),sQuery(id+"F0.wireOp",EDGE,"E57.MirrorCS"),sQuery(id+"F0.wireOp",EDGE,"E58.MirrorCS"),sQuery(id+"F0.wireOp",EDGE,"E59.MirrorCS"),sQuery(id+"F0.wireOp",EDGE,"E60.MirrorCS"),sQuery(id+"F0.wireOp",EDGE,"E61.MirrorCS"),sQuery(id+"F0.wireOp",EDGE,"E62.MirrorCS"),sQuery(id+"F0.wireOp",EDGE,"E63.MirrorCS"),sQuery(id+"F0.wireOp",EDGE,"E64.MirrorCS"),sQuery(id+"F0.wireOp",EDGE,"E65.MirrorCS"),sQuery(id+"F0.wireOp",EDGE,"E66.MirrorCS"),sQuery(id+"F0.wireOp",EDGE,"E67.MirrorCS"),sQuery(id+"F0.wireOp",EDGE,"E68.MirrorCS"),sQuery(id+"F0.wireOp",EDGE,"E69.MirrorCS"),sQuery(id+"F0.wireOp",EDGE,"E70.MirrorCS"),sQuery(id+"F0.wireOp",EDGE,"E71.MirrorCS"),sQuery(id+"F0.wireOp",EDGE,"E72.MirrorCS"),sQuery(id+"F0.wireOp",EDGE,"E73.MirrorCS"),sQuery(id+"F0.wireOp",EDGE,"E74.MirrorCS"),sQuery(id+"F0.wireOp",EDGE,"E75.MirrorCS"),sQuery(id+"F0.wireOp",EDGE,"E76.MirrorCS"),sQuery(id+"F0.wireOp",EDGE,"E77.MirrorCS"),sQuery(id+"F0.wireOp",EDGE,"E78.MirrorCS"),sQuery(id+"F0.wireOp",EDGE,"E79.MirrorCS"),sQuery(id+"F0.wireOp",EDGE,"E80.MirrorCS"),sQuery(id+"F0.wireOp",EDGE,"E81.MirrorCS"),sQuery(id+"F0.wireOp",EDGE,"E82.trimOffspring"),sQuery(id+"F0.wireOp",EDGE,"E83.trimOffspring")])],"isStart":false});
            var sketch = newSketch(context, id + "F2", { "sketchPlane" : qUnion([Q0])});
            skCircle(sketch, "E84", {"center": v(0, 0) * mm, "radius": 27.5 * mm});
            skSolve(sketch);
        }
        {
            var Q0;
            Q0=qSketchRegion(id+"F2",true);
            extrude(context, id + "F3", {"entities" : qUnion([Q0]), "operationType" : NewBodyOperationType.ADD, "depth" : 15 * mm, "offsetDistance" : 25 * mm});
        }
        {
            var Q0;
            Q0=makeQuery(id+"F3.opExtrude","CAP_FACE",FACE,{"disambiguationData":[OSD([sQuery(id+"F2.wireOp",EDGE,"E84")])],"isStart":false});
            var sketch = newSketch(context, id + "F4", { "sketchPlane" : qUnion([Q0])});
            skCircle(sketch, "E85", {"center": v(0, 0) * mm, "radius": 7 * mm});
            skSolve(sketch);
        }
        {
            var Q0;
            Q0=qSketchRegion(id+"F4",true);
            extrude(context, id + "F5", {"entities" : qUnion([Q0]), "operationType" : NewBodyOperationType.REMOVE, "endBound" : BoundingType.UP_TO_NEXT, "oppositeDirection" : true, "depth" : 25 * mm, "offsetDistance" : 25 * mm});
        }
        {
            var Q0;
            Q0=makeQuery(id+"F3.opExtrude","SWEPT_FACE",FACE,{"disambiguationData":[OSD([sQuery(id+"F2.wireOp",EDGE,"E84")])]});
            var Q1;
            Q1=makeQuery(id+"F5.boolean.opBoolean","COPY",FACE,{"derivedFrom":makeQuery(id+"F5.opExtrude","SWEPT_FACE",FACE,{"disambiguationData":[OSD([sQuery(id+"F4.wireOp",EDGE,"E85")])]})});
            chamfer(context, id + "F6", {"entities" : qUnion([Q0, Q1]), "width" : 1 * mm, "tangentPropagation" : true});
        }
        {
            var Q0;
            Q0=makeQuery(id+"F3.opExtrude","CAP_FACE",FACE,{"disambiguationData":[OSD([sQuery(id+"F2.wireOp",EDGE,"E84")])],"isStart":false});
            var sketch = newSketch(context, id + "F7", { "sketchPlane" : qUnion([Q0])});
            skFitSpline(sketch, "E86.0.26", {"points": [v(3.68, 35.05) * mm, v(3.69, 35.2) * mm, v(3.7, 35.63) * mm, v(3.44, 37.3) * mm, v(2.57, 39.8) * mm, v(0.74, 43.12) * mm, v(-2.3, 46.88) * mm, v(-6.8, 50.76) * mm, v(-12.75, 54.43) * mm, v(-17.73, 56.13) * mm, v(-20.31, 57) * mm], "construction": true});
            skArc(sketch, "E86.0.27", {"start": v(2.42, 39.93) * mm, "mid": v(1.5, 39.97) * mm, "end": v(0.6, 40) * mm, "construction": true});
            skFitSpline(sketch, "E86.0.28", {"points": [v(24.54, 55.32) * mm, v(21.9, 54.64) * mm, v(16.8, 53.32) * mm, v(10.59, 50.1) * mm, v(5.82, 46.58) * mm, v(2.5, 43.05) * mm, v(0.43, 39.89) * mm, v(-0.63, 37.46) * mm, v(-1.01, 35.8) * mm, v(-1.03, 35.38) * mm, v(-1.04, 35.22) * mm], "construction": true});
            skFitSpline(sketch, "E86.0.84", {"points": [v(-52.45, 30.19) * mm, v(-52.05, 27.5) * mm, v(-51.27, 22.28) * mm, v(-48.72, 15.76) * mm, v(-45.71, 10.66) * mm, v(-42.56, 6.99) * mm, v(-39.63, 4.6) * mm, v(-37.32, 3.29) * mm, v(-35.72, 2.74) * mm, v(-35.3, 2.67) * mm, v(-35.14, 2.65) * mm], "construction": true});
            skLineSegment(sketch, "E86.0.85", {"start": v(-35.14, 2.65) * mm, "end": v(-34.9, 2.63) * mm, "construction": true});
            skArc(sketch, "E86.0.86", {"start": v(-34.9, 2.63) * mm, "mid": v(-34.56, 2.46) * mm, "end": v(-34.44, 2.1) * mm, "construction": true});
            skArc(sketch, "E86.0.87", {"start": v(-34.44, 2.1) * mm, "mid": v(-34.48, 1.3) * mm, "end": v(-34.5, 0.5) * mm, "construction": true});
            skArc(sketch, "E86.0.88", {"start": v(-34.5, 0.5) * mm, "mid": v(-34.65, 0.14) * mm, "end": v(-35, 0) * mm, "construction": true});
            skLineSegment(sketch, "E86.0.89", {"start": v(-35, 0) * mm, "end": v(-35.24, 0) * mm, "construction": true});
            skFitSpline(sketch, "E86.0.90", {"points": [v(-35.24, 0) * mm, v(-35.4, -0.01) * mm, v(-35.82, -0.04) * mm, v(-37.46, -0.47) * mm, v(-39.86, -1.6) * mm, v(-42.96, -3.77) * mm, v(-46.39, -7.2) * mm, v(-49.77, -12.06) * mm, v(-52.8, -18.37) * mm, v(-53.97, -23.5) * mm, v(-54.57, -26.16) * mm], "construction": true});
            skFitSpline(sketch, "E86.0.146", {"points": [v(-3.68, -35.05) * mm, v(-3.69, -35.2) * mm, v(-3.7, -35.63) * mm, v(-3.44, -37.3) * mm, v(-2.57, -39.8) * mm, v(-0.74, -43.12) * mm, v(2.3, -46.88) * mm, v(6.8, -50.76) * mm, v(12.75, -54.43) * mm, v(17.73, -56.13) * mm, v(20.31, -57) * mm], "construction": true});
            skArc(sketch, "E86.0.147", {"start": v(-2.42, -39.93) * mm, "mid": v(-1.5, -39.97) * mm, "end": v(-0.6, -40) * mm, "construction": true});
            skFitSpline(sketch, "E86.0.148", {"points": [v(-24.54, -55.32) * mm, v(-21.9, -54.64) * mm, v(-16.8, -53.32) * mm, v(-10.59, -50.1) * mm, v(-5.82, -46.58) * mm, v(-2.5, -43.05) * mm, v(-0.43, -39.89) * mm, v(0.63, -37.46) * mm, v(1.01, -35.8) * mm, v(1.03, -35.38) * mm, v(1.04, -35.22) * mm], "construction": true});
            skFitSpline(sketch, "E86.0.204", {"points": [v(52.45, -30.19) * mm, v(52.05, -27.5) * mm, v(51.27, -22.28) * mm, v(48.72, -15.76) * mm, v(45.71, -10.66) * mm, v(42.56, -6.99) * mm, v(39.63, -4.6) * mm, v(37.32, -3.29) * mm, v(35.72, -2.74) * mm, v(35.3, -2.67) * mm, v(35.14, -2.65) * mm], "construction": true});
            skLineSegment(sketch, "E86.0.205", {"start": v(35.14, -2.65) * mm, "end": v(34.9, -2.63) * mm, "construction": true});
            skArc(sketch, "E86.0.206", {"start": v(34.9, -2.63) * mm, "mid": v(34.56, -2.46) * mm, "end": v(34.44, -2.1) * mm, "construction": true});
            skArc(sketch, "E86.0.207", {"start": v(34.44, -2.1) * mm, "mid": v(34.48, -1.3) * mm, "end": v(34.5, -0.5) * mm, "construction": true});
            skArc(sketch, "E86.0.208", {"start": v(34.5, -0.5) * mm, "mid": v(34.65, -0.14) * mm, "end": v(35, 0) * mm, "construction": true});
            skLineSegment(sketch, "E86.0.209", {"start": v(35, 0) * mm, "end": v(35.24, 0) * mm, "construction": true});
            skFitSpline(sketch, "E86.0.210", {"points": [v(35.24, 0) * mm, v(35.4, 0.01) * mm, v(35.82, 0.04) * mm, v(37.46, 0.47) * mm, v(39.86, 1.6) * mm, v(42.96, 3.77) * mm, v(46.39, 7.2) * mm, v(49.77, 12.06) * mm, v(52.8, 18.37) * mm, v(53.97, 23.5) * mm, v(54.57, 26.16) * mm], "construction": true});
            skLineSegment(sketch, "E87", {"start": v(1.5, 39.97) * mm, "end": v(-1.5, -39.97) * mm, "construction": true});
            skLineSegment(sketch, "E88", {"start": v(34.5, -1.3) * mm, "end": v(-34.48, 1.3) * mm, "construction": true});
            skPoint(sketch, "E88.startSnap0", {"position": v(34.48, -1.3) * mm});
            skLineSegment(sketch, "E89.0", {"start": v(4.5, 39.86) * mm, "end": v(1.5, -40.08) * mm, "construction": true});
            skLineSegment(sketch, "E90.0", {"start": v(-1.5, 40.08) * mm, "end": v(-4.5, -39.86) * mm, "construction": true});
            skLineSegment(sketch, "E91.0", {"start": v(34.86, 8.5) * mm, "end": v(-34.1, 11.1) * mm, "construction": true});
            skLineSegment(sketch, "E92", {"start": v(-2.63, 9.9) * mm, "end": v(3.37, 9.68) * mm});
            skLineSegment(sketch, "E93", {"start": v(3.37, 9.68) * mm, "end": v(3, -0.11) * mm});
            skLineSegment(sketch, "E94", {"start": v(3, -0.11) * mm, "end": v(-3, 0.11) * mm});
            skLineSegment(sketch, "E95", {"start": v(-3, 0.11) * mm, "end": v(-2.63, 9.9) * mm});
            skSolve(sketch);
        }
        {
            var Q0;
            Q0=qSketchRegion(id+"F7",true);
            extrude(context, id + "F8", {"entities" : qUnion([Q0]), "operationType" : NewBodyOperationType.REMOVE, "endBound" : BoundingType.THROUGH_ALL, "oppositeDirection" : true, "depth" : 25 * mm, "offsetDistance" : 25 * mm});
        }
    });
